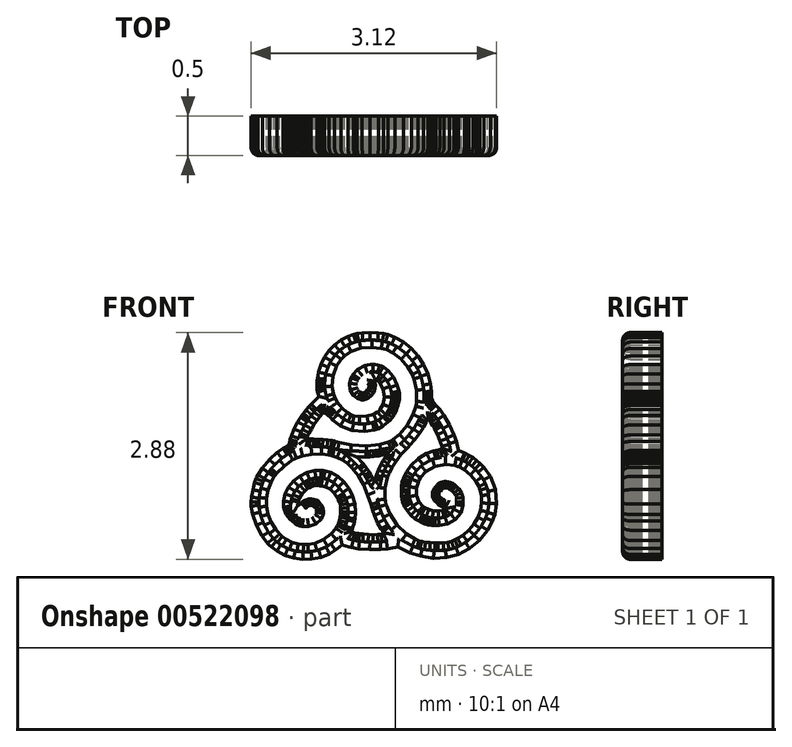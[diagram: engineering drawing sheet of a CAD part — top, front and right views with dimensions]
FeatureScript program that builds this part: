
annotation { "Feature Type Name" : "Feature", "Feature Type Description" : "" }
export const myFeature = defineFeature(function(context is Context, id is Id, definition is map)
    precondition{}
    {
        {
            var Q0;
            Q0=qCreatedBy(makeId("Front.planeOp"),FACE);
            var sketch = newSketch(context, id + "F0", { "sketchPlane" : qUnion([Q0])});
            skLineSegment(sketch, "E0", {"start": v(-0.23, 1.42) * mm, "end": v(-0.26, 1.42) * mm});
            skLineSegment(sketch, "E1", {"start": v(-0.26, 1.42) * mm, "end": v(-0.33, 1.4) * mm});
            skLineSegment(sketch, "E2", {"start": v(-0.33, 1.4) * mm, "end": v(-0.42, 1.34) * mm});
            skLineSegment(sketch, "E3", {"start": v(-0.42, 1.34) * mm, "end": v(-0.5, 1.28) * mm});
            skLineSegment(sketch, "E4", {"start": v(-0.5, 1.28) * mm, "end": v(-0.57, 1.21) * mm});
            skLineSegment(sketch, "E5", {"start": v(-0.57, 1.21) * mm, "end": v(-0.63, 1.13) * mm});
            skLineSegment(sketch, "E6", {"start": v(-0.63, 1.13) * mm, "end": v(-0.67, 1.04) * mm});
            skLineSegment(sketch, "E7", {"start": v(-0.67, 1.04) * mm, "end": v(-0.7, 0.94) * mm});
            skLineSegment(sketch, "E8", {"start": v(-0.7, 0.94) * mm, "end": v(-0.72, 0.86) * mm});
            skLineSegment(sketch, "E9", {"start": v(-0.72, 0.86) * mm, "end": v(-0.72, 0.83) * mm});
            skLineSegment(sketch, "E10", {"start": v(-0.72, 0.83) * mm, "end": v(-0.72, 0.82) * mm});
            skLineSegment(sketch, "E11", {"start": v(-0.72, 0.82) * mm, "end": v(-0.72, 0.8) * mm});
            skLineSegment(sketch, "E12", {"start": v(-0.72, 0.8) * mm, "end": v(-0.72, 0.75) * mm});
            skLineSegment(sketch, "E13", {"start": v(-0.72, 0.75) * mm, "end": v(-0.72, 0.71) * mm});
            skLineSegment(sketch, "E14", {"start": v(-0.72, 0.71) * mm, "end": v(-0.72, 0.7) * mm});
            skLineSegment(sketch, "E15", {"start": v(-0.72, 0.7) * mm, "end": v(-0.71, 0.69) * mm});
            skLineSegment(sketch, "E16", {"start": v(-0.71, 0.69) * mm, "end": v(-0.7, 0.63) * mm});
            skLineSegment(sketch, "E17", {"start": v(-0.7, 0.63) * mm, "end": v(-0.79, 0.54) * mm});
            skLineSegment(sketch, "E18", {"start": v(-0.79, 0.54) * mm, "end": v(-0.8, 0.53) * mm});
            skLineSegment(sketch, "E19", {"start": v(-0.8, 0.53) * mm, "end": v(-0.83, 0.5) * mm});
            skLineSegment(sketch, "E20", {"start": v(-0.83, 0.5) * mm, "end": v(-0.86, 0.46) * mm});
            skLineSegment(sketch, "E21", {"start": v(-0.86, 0.46) * mm, "end": v(-0.9, 0.42) * mm});
            skLineSegment(sketch, "E22", {"start": v(-0.9, 0.42) * mm, "end": v(-0.91, 0.4) * mm});
            skLineSegment(sketch, "E23", {"start": v(-0.91, 0.4) * mm, "end": v(-0.92, 0.38) * mm});
            skLineSegment(sketch, "E24", {"start": v(-0.92, 0.38) * mm, "end": v(-0.93, 0.36) * mm});
            skLineSegment(sketch, "E25", {"start": v(-0.93, 0.36) * mm, "end": v(-0.97, 0.3) * mm});
            skLineSegment(sketch, "E26", {"start": v(-0.97, 0.3) * mm, "end": v(-1.01, 0.22) * mm});
            skLineSegment(sketch, "E27", {"start": v(-1.01, 0.22) * mm, "end": v(-1.05, 0.13) * mm});
            skLineSegment(sketch, "E28", {"start": v(-1.05, 0.13) * mm, "end": v(-1.06, 0.08) * mm});
            skLineSegment(sketch, "E29", {"start": v(-1.06, 0.08) * mm, "end": v(-1.07, 0.06) * mm});
            skLineSegment(sketch, "E30", {"start": v(-1.07, 0.06) * mm, "end": v(-1.07, 0.06) * mm});
            skLineSegment(sketch, "E31", {"start": v(-1.07, 0.06) * mm, "end": v(-1.07, 0.04) * mm});
            skLineSegment(sketch, "E32", {"start": v(-1.07, 0.04) * mm, "end": v(-1.09, 0.02) * mm});
            skLineSegment(sketch, "E33", {"start": v(-1.09, 0.02) * mm, "end": v(-1.1, 0) * mm});
            skLineSegment(sketch, "E34", {"start": v(-1.1, 0) * mm, "end": v(-1.12, -0.01) * mm});
            skLineSegment(sketch, "E35", {"start": v(-1.12, -0.01) * mm, "end": v(-1.13, -0.02) * mm});
            skLineSegment(sketch, "E36", {"start": v(-1.13, -0.02) * mm, "end": v(-1.15, -0.03) * mm});
            skLineSegment(sketch, "E37", {"start": v(-1.15, -0.03) * mm, "end": v(-1.23, -0.08) * mm});
            skLineSegment(sketch, "E38", {"start": v(-1.23, -0.08) * mm, "end": v(-1.33, -0.17) * mm});
            skLineSegment(sketch, "E39", {"start": v(-1.33, -0.17) * mm, "end": v(-1.42, -0.28) * mm});
            skLineSegment(sketch, "E40", {"start": v(-1.42, -0.28) * mm, "end": v(-1.47, -0.37) * mm});
            skLineSegment(sketch, "E41", {"start": v(-1.47, -0.37) * mm, "end": v(-1.49, -0.4) * mm});
            skLineSegment(sketch, "E42", {"start": v(-1.49, -0.4) * mm, "end": v(-1.5, -0.41) * mm});
            skLineSegment(sketch, "E43", {"start": v(-1.5, -0.41) * mm, "end": v(-1.51, -0.47) * mm});
            skLineSegment(sketch, "E44", {"start": v(-1.51, -0.47) * mm, "end": v(-1.54, -0.56) * mm});
            skLineSegment(sketch, "E45", {"start": v(-1.54, -0.56) * mm, "end": v(-1.55, -0.65) * mm});
            skLineSegment(sketch, "E46", {"start": v(-1.55, -0.65) * mm, "end": v(-1.56, -0.7) * mm});
            skLineSegment(sketch, "E47", {"start": v(-1.56, -0.7) * mm, "end": v(-1.56, -0.73) * mm});
            skLineSegment(sketch, "E48", {"start": v(-1.56, -0.73) * mm, "end": v(-1.56, -0.76) * mm});
            skLineSegment(sketch, "E49", {"start": v(-1.56, -0.76) * mm, "end": v(-1.54, -0.86) * mm});
            skLineSegment(sketch, "E50", {"start": v(-1.54, -0.86) * mm, "end": v(-1.5, -1) * mm});
            skLineSegment(sketch, "E51", {"start": v(-1.5, -1) * mm, "end": v(-1.42, -1.14) * mm});
            skLineSegment(sketch, "E52", {"start": v(-1.42, -1.14) * mm, "end": v(-1.35, -1.24) * mm});
            skLineSegment(sketch, "E53", {"start": v(-1.35, -1.24) * mm, "end": v(-1.32, -1.26) * mm});
            skLineSegment(sketch, "E54", {"start": v(-1.32, -1.26) * mm, "end": v(-1.3, -1.28) * mm});
            skLineSegment(sketch, "E55", {"start": v(-1.3, -1.28) * mm, "end": v(-1.23, -1.34) * mm});
            skLineSegment(sketch, "E56", {"start": v(-1.23, -1.34) * mm, "end": v(-1.13, -1.39) * mm});
            skLineSegment(sketch, "E57", {"start": v(-1.13, -1.39) * mm, "end": v(-1.02, -1.43) * mm});
            skLineSegment(sketch, "E58", {"start": v(-1.02, -1.43) * mm, "end": v(-0.9, -1.44) * mm});
            skLineSegment(sketch, "E59", {"start": v(-0.9, -1.44) * mm, "end": v(-0.79, -1.44) * mm});
            skLineSegment(sketch, "E60", {"start": v(-0.79, -1.44) * mm, "end": v(-0.67, -1.41) * mm});
            skLineSegment(sketch, "E61", {"start": v(-0.67, -1.41) * mm, "end": v(-0.56, -1.37) * mm});
            skLineSegment(sketch, "E62", {"start": v(-0.56, -1.37) * mm, "end": v(-0.49, -1.32) * mm});
            skLineSegment(sketch, "E63", {"start": v(-0.49, -1.32) * mm, "end": v(-0.47, -1.3) * mm});
            skLineSegment(sketch, "E64", {"start": v(-0.47, -1.3) * mm, "end": v(-0.4, -1.26) * mm});
            skLineSegment(sketch, "E65", {"start": v(-0.4, -1.26) * mm, "end": v(-0.31, -1.28) * mm});
            skLineSegment(sketch, "E66", {"start": v(-0.31, -1.28) * mm, "end": v(-0.28, -1.3) * mm});
            skLineSegment(sketch, "E67", {"start": v(-0.28, -1.3) * mm, "end": v(-0.2, -1.3) * mm});
            skLineSegment(sketch, "E68", {"start": v(-0.2, -1.3) * mm, "end": v(-0.05, -1.32) * mm});
            skLineSegment(sketch, "E69", {"start": v(-0.05, -1.32) * mm, "end": v(0.09, -1.32) * mm});
            skLineSegment(sketch, "E70", {"start": v(0.09, -1.32) * mm, "end": v(0.17, -1.3) * mm});
            skLineSegment(sketch, "E71", {"start": v(0.17, -1.3) * mm, "end": v(0.2, -1.3) * mm});
            skLineSegment(sketch, "E72", {"start": v(0.2, -1.3) * mm, "end": v(0.3, -1.28) * mm});
            skLineSegment(sketch, "E73", {"start": v(0.3, -1.28) * mm, "end": v(0.42, -1.34) * mm});
            skLineSegment(sketch, "E74", {"start": v(0.42, -1.34) * mm, "end": v(0.46, -1.36) * mm});
            skLineSegment(sketch, "E75", {"start": v(0.46, -1.36) * mm, "end": v(0.6, -1.4) * mm});
            skLineSegment(sketch, "E76", {"start": v(0.6, -1.4) * mm, "end": v(0.76, -1.43) * mm});
            skLineSegment(sketch, "E77", {"start": v(0.76, -1.43) * mm, "end": v(0.92, -1.42) * mm});
            skLineSegment(sketch, "E78", {"start": v(0.92, -1.42) * mm, "end": v(1.08, -1.38) * mm});
            skLineSegment(sketch, "E79", {"start": v(1.08, -1.38) * mm, "end": v(1.22, -1.3) * mm});
            skLineSegment(sketch, "E80", {"start": v(1.22, -1.3) * mm, "end": v(1.34, -1.2) * mm});
            skLineSegment(sketch, "E81", {"start": v(1.34, -1.2) * mm, "end": v(1.44, -1.07) * mm});
            skLineSegment(sketch, "E82", {"start": v(1.44, -1.07) * mm, "end": v(1.5, -0.95) * mm});
            skLineSegment(sketch, "E83", {"start": v(1.5, -0.95) * mm, "end": v(1.52, -0.91) * mm});
            skLineSegment(sketch, "E84", {"start": v(1.52, -0.91) * mm, "end": v(1.54, -0.87) * mm});
            skLineSegment(sketch, "E85", {"start": v(1.54, -0.87) * mm, "end": v(1.56, -0.73) * mm});
            skLineSegment(sketch, "E86", {"start": v(1.56, -0.73) * mm, "end": v(1.54, -0.55) * mm});
            skLineSegment(sketch, "E87", {"start": v(1.54, -0.55) * mm, "end": v(1.48, -0.39) * mm});
            skLineSegment(sketch, "E88", {"start": v(1.48, -0.39) * mm, "end": v(1.4, -0.27) * mm});
            skLineSegment(sketch, "E89", {"start": v(1.4, -0.27) * mm, "end": v(1.37, -0.24) * mm});
            skLineSegment(sketch, "E90", {"start": v(1.37, -0.24) * mm, "end": v(1.35, -0.22) * mm});
            skLineSegment(sketch, "E91", {"start": v(1.35, -0.22) * mm, "end": v(1.3, -0.18) * mm});
            skLineSegment(sketch, "E92", {"start": v(1.3, -0.18) * mm, "end": v(1.26, -0.15) * mm});
            skLineSegment(sketch, "E93", {"start": v(1.26, -0.15) * mm, "end": v(1.21, -0.12) * mm});
            skLineSegment(sketch, "E94", {"start": v(1.21, -0.12) * mm, "end": v(1.17, -0.1) * mm});
            skLineSegment(sketch, "E95", {"start": v(1.17, -0.1) * mm, "end": v(1.15, -0.1) * mm});
            skLineSegment(sketch, "E96", {"start": v(1.15, -0.1) * mm, "end": v(1.07, -0.06) * mm});
            skLineSegment(sketch, "E97", {"start": v(1.07, -0.06) * mm, "end": v(1.06, 0.03) * mm});
            skLineSegment(sketch, "E98", {"start": v(1.06, 0.03) * mm, "end": v(1.05, 0.06) * mm});
            skLineSegment(sketch, "E99", {"start": v(1.05, 0.06) * mm, "end": v(1.02, 0.14) * mm});
            skLineSegment(sketch, "E100", {"start": v(1.02, 0.14) * mm, "end": v(0.96, 0.27) * mm});
            skLineSegment(sketch, "E101", {"start": v(0.96, 0.27) * mm, "end": v(0.9, 0.39) * mm});
            skLineSegment(sketch, "E102", {"start": v(0.9, 0.39) * mm, "end": v(0.84, 0.46) * mm});
            skLineSegment(sketch, "E103", {"start": v(0.84, 0.46) * mm, "end": v(0.82, 0.49) * mm});
            skLineSegment(sketch, "E104", {"start": v(0.82, 0.49) * mm, "end": v(0.8, 0.5) * mm});
            skLineSegment(sketch, "E105", {"start": v(0.8, 0.5) * mm, "end": v(0.79, 0.52) * mm});
            skLineSegment(sketch, "E106", {"start": v(0.79, 0.52) * mm, "end": v(0.77, 0.54) * mm});
            skLineSegment(sketch, "E107", {"start": v(0.77, 0.54) * mm, "end": v(0.75, 0.56) * mm});
            skLineSegment(sketch, "E108", {"start": v(0.75, 0.56) * mm, "end": v(0.74, 0.58) * mm});
            skLineSegment(sketch, "E109", {"start": v(0.74, 0.58) * mm, "end": v(0.74, 0.6) * mm});
            skLineSegment(sketch, "E110", {"start": v(0.74, 0.6) * mm, "end": v(0.73, 0.61) * mm});
            skLineSegment(sketch, "E111", {"start": v(0.73, 0.61) * mm, "end": v(0.73, 0.63) * mm});
            skLineSegment(sketch, "E112", {"start": v(0.73, 0.63) * mm, "end": v(0.73, 0.65) * mm});
            skLineSegment(sketch, "E113", {"start": v(0.73, 0.65) * mm, "end": v(0.73, 0.66) * mm});
            skLineSegment(sketch, "E114", {"start": v(0.73, 0.66) * mm, "end": v(0.73, 0.7) * mm});
            skLineSegment(sketch, "E115", {"start": v(0.73, 0.7) * mm, "end": v(0.72, 0.8) * mm});
            skLineSegment(sketch, "E116", {"start": v(0.72, 0.8) * mm, "end": v(0.69, 0.92) * mm});
            skLineSegment(sketch, "E117", {"start": v(0.69, 0.92) * mm, "end": v(0.63, 1.03) * mm});
            skLineSegment(sketch, "E118", {"start": v(0.63, 1.03) * mm, "end": v(0.56, 1.14) * mm});
            skLineSegment(sketch, "E119", {"start": v(0.56, 1.14) * mm, "end": v(0.48, 1.24) * mm});
            skLineSegment(sketch, "E120", {"start": v(0.48, 1.24) * mm, "end": v(0.38, 1.32) * mm});
            skLineSegment(sketch, "E121", {"start": v(0.38, 1.32) * mm, "end": v(0.27, 1.38) * mm});
            skLineSegment(sketch, "E122", {"start": v(0.27, 1.38) * mm, "end": v(0.18, 1.41) * mm});
            skLineSegment(sketch, "E123", {"start": v(0.18, 1.41) * mm, "end": v(0.15, 1.42) * mm});
            skLineSegment(sketch, "E124", {"start": v(0.15, 1.42) * mm, "end": v(0.13, 1.43) * mm});
            skLineSegment(sketch, "E125", {"start": v(0.13, 1.43) * mm, "end": v(0.06, 1.44) * mm});
            skLineSegment(sketch, "E126", {"start": v(0.06, 1.44) * mm, "end": v(-0.05, 1.44) * mm});
            skLineSegment(sketch, "E127", {"start": v(-0.05, 1.44) * mm, "end": v(-0.15, 1.44) * mm});
            skLineSegment(sketch, "E128", {"start": v(-0.15, 1.44) * mm, "end": v(-0.21, 1.43) * mm});
            skLineSegment(sketch, "E129", {"start": v(-0.21, 1.43) * mm, "end": v(-0.23, 1.42) * mm});
            skLineSegment(sketch, "E130", {"start": v(0.13, 1.23) * mm, "end": v(0.16, 1.22) * mm});
            skLineSegment(sketch, "E131", {"start": v(0.16, 1.22) * mm, "end": v(0.24, 1.18) * mm});
            skLineSegment(sketch, "E132", {"start": v(0.24, 1.18) * mm, "end": v(0.35, 1.1) * mm});
            skLineSegment(sketch, "E133", {"start": v(0.35, 1.1) * mm, "end": v(0.44, 1) * mm});
            skLineSegment(sketch, "E134", {"start": v(0.44, 1) * mm, "end": v(0.49, 0.9) * mm});
            skLineSegment(sketch, "E135", {"start": v(0.49, 0.9) * mm, "end": v(0.5, 0.88) * mm});
            skLineSegment(sketch, "E136", {"start": v(0.5, 0.88) * mm, "end": v(0.5, 0.85) * mm});
            skLineSegment(sketch, "E137", {"start": v(0.5, 0.85) * mm, "end": v(0.54, 0.7) * mm});
            skLineSegment(sketch, "E138", {"start": v(0.54, 0.7) * mm, "end": v(0.54, 0.57) * mm});
            skLineSegment(sketch, "E139", {"start": v(0.54, 0.57) * mm, "end": v(0.54, 0.54) * mm});
            skLineSegment(sketch, "E140", {"start": v(0.54, 0.54) * mm, "end": v(0.53, 0.5) * mm});
            skLineSegment(sketch, "E141", {"start": v(0.53, 0.5) * mm, "end": v(0.5, 0.4) * mm});
            skLineSegment(sketch, "E142", {"start": v(0.5, 0.4) * mm, "end": v(0.42, 0.26) * mm});
            skLineSegment(sketch, "E143", {"start": v(0.42, 0.26) * mm, "end": v(0.32, 0.15) * mm});
            skLineSegment(sketch, "E144", {"start": v(0.32, 0.15) * mm, "end": v(0.25, 0.08) * mm});
            skLineSegment(sketch, "E145", {"start": v(0.25, 0.08) * mm, "end": v(0.22, 0.07) * mm});
            skLineSegment(sketch, "E146", {"start": v(0.22, 0.07) * mm, "end": v(0.18, 0.05) * mm});
            skLineSegment(sketch, "E147", {"start": v(0.18, 0.05) * mm, "end": v(0.08, 0.02) * mm});
            skLineSegment(sketch, "E148", {"start": v(0.08, 0.02) * mm, "end": v(-0.1, 0) * mm});
            skLineSegment(sketch, "E149", {"start": v(-0.1, 0) * mm, "end": v(-0.28, 0.02) * mm});
            skLineSegment(sketch, "E150", {"start": v(-0.28, 0.02) * mm, "end": v(-0.44, 0.05) * mm});
            skLineSegment(sketch, "E151", {"start": v(-0.44, 0.05) * mm, "end": v(-0.5, 0.06) * mm});
            skLineSegment(sketch, "E152", {"start": v(-0.5, 0.06) * mm, "end": v(-0.5, 0.06) * mm});
            skLineSegment(sketch, "E153", {"start": v(-0.5, 0.06) * mm, "end": v(-0.53, 0.07) * mm});
            skLineSegment(sketch, "E154", {"start": v(-0.53, 0.07) * mm, "end": v(-0.59, 0.08) * mm});
            skLineSegment(sketch, "E155", {"start": v(-0.59, 0.08) * mm, "end": v(-0.65, 0.08) * mm});
            skLineSegment(sketch, "E156", {"start": v(-0.65, 0.08) * mm, "end": v(-0.7, 0.09) * mm});
            skLineSegment(sketch, "E157", {"start": v(-0.7, 0.09) * mm, "end": v(-0.7, 0.09) * mm});
            skLineSegment(sketch, "E158", {"start": v(-0.7, 0.09) * mm, "end": v(-0.72, 0.09) * mm});
            skLineSegment(sketch, "E159", {"start": v(-0.72, 0.09) * mm, "end": v(-0.76, 0.09) * mm});
            skLineSegment(sketch, "E160", {"start": v(-0.76, 0.09) * mm, "end": v(-0.8, 0.1) * mm});
            skLineSegment(sketch, "E161", {"start": v(-0.8, 0.1) * mm, "end": v(-0.84, 0.1) * mm});
            skLineSegment(sketch, "E162", {"start": v(-0.84, 0.1) * mm, "end": v(-0.85, 0.1) * mm});
            skLineSegment(sketch, "E163", {"start": v(-0.85, 0.1) * mm, "end": v(-0.85, 0.1) * mm});
            skLineSegment(sketch, "E164", {"start": v(-0.85, 0.1) * mm, "end": v(-0.84, 0.12) * mm});
            skLineSegment(sketch, "E165", {"start": v(-0.84, 0.12) * mm, "end": v(-0.82, 0.17) * mm});
            skLineSegment(sketch, "E166", {"start": v(-0.82, 0.17) * mm, "end": v(-0.8, 0.22) * mm});
            skLineSegment(sketch, "E167", {"start": v(-0.8, 0.22) * mm, "end": v(-0.76, 0.27) * mm});
            skLineSegment(sketch, "E168", {"start": v(-0.76, 0.27) * mm, "end": v(-0.72, 0.33) * mm});
            skLineSegment(sketch, "E169", {"start": v(-0.72, 0.33) * mm, "end": v(-0.69, 0.37) * mm});
            skLineSegment(sketch, "E170", {"start": v(-0.69, 0.37) * mm, "end": v(-0.66, 0.4) * mm});
            skLineSegment(sketch, "E171", {"start": v(-0.66, 0.4) * mm, "end": v(-0.64, 0.42) * mm});
            skLineSegment(sketch, "E172", {"start": v(-0.64, 0.42) * mm, "end": v(-0.64, 0.42) * mm});
            skLineSegment(sketch, "E173", {"start": v(-0.64, 0.42) * mm, "end": v(-0.63, 0.43) * mm});
            skLineSegment(sketch, "E174", {"start": v(-0.63, 0.43) * mm, "end": v(-0.62, 0.42) * mm});
            skLineSegment(sketch, "E175", {"start": v(-0.62, 0.42) * mm, "end": v(-0.6, 0.4) * mm});
            skLineSegment(sketch, "E176", {"start": v(-0.6, 0.4) * mm, "end": v(-0.58, 0.39) * mm});
            skLineSegment(sketch, "E177", {"start": v(-0.58, 0.39) * mm, "end": v(-0.56, 0.37) * mm});
            skLineSegment(sketch, "E178", {"start": v(-0.56, 0.37) * mm, "end": v(-0.55, 0.36) * mm});
            skLineSegment(sketch, "E179", {"start": v(-0.55, 0.36) * mm, "end": v(-0.52, 0.33) * mm});
            skLineSegment(sketch, "E180", {"start": v(-0.52, 0.33) * mm, "end": v(-0.42, 0.26) * mm});
            skLineSegment(sketch, "E181", {"start": v(-0.42, 0.26) * mm, "end": v(-0.28, 0.2) * mm});
            skLineSegment(sketch, "E182", {"start": v(-0.28, 0.2) * mm, "end": v(-0.12, 0.18) * mm});
            skLineSegment(sketch, "E183", {"start": v(-0.12, 0.18) * mm, "end": v(0, 0.2) * mm});
            skLineSegment(sketch, "E184", {"start": v(0, 0.2) * mm, "end": v(0.04, 0.21) * mm});
            skLineSegment(sketch, "E185", {"start": v(0.04, 0.21) * mm, "end": v(0.06, 0.22) * mm});
            skLineSegment(sketch, "E186", {"start": v(0.06, 0.22) * mm, "end": v(0.12, 0.25) * mm});
            skLineSegment(sketch, "E187", {"start": v(0.12, 0.25) * mm, "end": v(0.18, 0.3) * mm});
            skLineSegment(sketch, "E188", {"start": v(0.18, 0.3) * mm, "end": v(0.2, 0.32) * mm});
            skLineSegment(sketch, "E189", {"start": v(0.2, 0.32) * mm, "end": v(0.2, 0.33) * mm});
            skLineSegment(sketch, "E190", {"start": v(0.2, 0.33) * mm, "end": v(0.23, 0.36) * mm});
            skLineSegment(sketch, "E191", {"start": v(0.23, 0.36) * mm, "end": v(0.26, 0.4) * mm});
            skLineSegment(sketch, "E192", {"start": v(0.26, 0.4) * mm, "end": v(0.28, 0.44) * mm});
            skLineSegment(sketch, "E193", {"start": v(0.28, 0.44) * mm, "end": v(0.3, 0.48) * mm});
            skLineSegment(sketch, "E194", {"start": v(0.3, 0.48) * mm, "end": v(0.3, 0.5) * mm});
            skLineSegment(sketch, "E195", {"start": v(0.3, 0.5) * mm, "end": v(0.3, 0.5) * mm});
            skLineSegment(sketch, "E196", {"start": v(0.3, 0.5) * mm, "end": v(0.32, 0.55) * mm});
            skLineSegment(sketch, "E197", {"start": v(0.32, 0.55) * mm, "end": v(0.32, 0.6) * mm});
            skLineSegment(sketch, "E198", {"start": v(0.32, 0.6) * mm, "end": v(0.33, 0.63) * mm});
            skLineSegment(sketch, "E199", {"start": v(0.33, 0.63) * mm, "end": v(0.32, 0.66) * mm});
            skLineSegment(sketch, "E200", {"start": v(0.32, 0.66) * mm, "end": v(0.32, 0.67) * mm});
            skLineSegment(sketch, "E201", {"start": v(0.32, 0.67) * mm, "end": v(0.32, 0.7) * mm});
            skLineSegment(sketch, "E202", {"start": v(0.32, 0.7) * mm, "end": v(0.3, 0.78) * mm});
            skLineSegment(sketch, "E203", {"start": v(0.3, 0.78) * mm, "end": v(0.25, 0.88) * mm});
            skLineSegment(sketch, "E204", {"start": v(0.25, 0.88) * mm, "end": v(0.18, 0.96) * mm});
            skLineSegment(sketch, "E205", {"start": v(0.18, 0.96) * mm, "end": v(0.12, 1) * mm});
            skLineSegment(sketch, "E206", {"start": v(0.12, 1) * mm, "end": v(0.1, 1.01) * mm});
            skLineSegment(sketch, "E207", {"start": v(0.1, 1.01) * mm, "end": v(0.07, 1.03) * mm});
            skLineSegment(sketch, "E208", {"start": v(0.07, 1.03) * mm, "end": v(0, 1.04) * mm});
            skLineSegment(sketch, "E209", {"start": v(0, 1.04) * mm, "end": v(-0.12, 1.02) * mm});
            skLineSegment(sketch, "E210", {"start": v(-0.12, 1.02) * mm, "end": v(-0.2, 0.97) * mm});
            skLineSegment(sketch, "E211", {"start": v(-0.2, 0.97) * mm, "end": v(-0.27, 0.91) * mm});
            skLineSegment(sketch, "E212", {"start": v(-0.27, 0.91) * mm, "end": v(-0.28, 0.89) * mm});
            skLineSegment(sketch, "E213", {"start": v(-0.28, 0.89) * mm, "end": v(-0.29, 0.87) * mm});
            skLineSegment(sketch, "E214", {"start": v(-0.29, 0.87) * mm, "end": v(-0.3, 0.8) * mm});
            skLineSegment(sketch, "E215", {"start": v(-0.3, 0.8) * mm, "end": v(-0.3, 0.71) * mm});
            skLineSegment(sketch, "E216", {"start": v(-0.3, 0.71) * mm, "end": v(-0.26, 0.64) * mm});
            skLineSegment(sketch, "E217", {"start": v(-0.26, 0.64) * mm, "end": v(-0.2, 0.6) * mm});
            skLineSegment(sketch, "E218", {"start": v(-0.2, 0.6) * mm, "end": v(-0.2, 0.6) * mm});
            skLineSegment(sketch, "E219", {"start": v(-0.2, 0.6) * mm, "end": v(-0.18, 0.6) * mm});
            skLineSegment(sketch, "E220", {"start": v(-0.18, 0.6) * mm, "end": v(-0.16, 0.59) * mm});
            skLineSegment(sketch, "E221", {"start": v(-0.16, 0.59) * mm, "end": v(-0.14, 0.59) * mm});
            skLineSegment(sketch, "E222", {"start": v(-0.14, 0.59) * mm, "end": v(-0.11, 0.59) * mm});
            skLineSegment(sketch, "E223", {"start": v(-0.11, 0.59) * mm, "end": v(-0.1, 0.6) * mm});
            skLineSegment(sketch, "E224", {"start": v(-0.1, 0.6) * mm, "end": v(-0.08, 0.6) * mm});
            skLineSegment(sketch, "E225", {"start": v(-0.08, 0.6) * mm, "end": v(-0.07, 0.6) * mm});
            skLineSegment(sketch, "E226", {"start": v(-0.07, 0.6) * mm, "end": v(-0.03, 0.63) * mm});
            skLineSegment(sketch, "E227", {"start": v(-0.03, 0.63) * mm, "end": v(0, 0.68) * mm});
            skLineSegment(sketch, "E228", {"start": v(0, 0.68) * mm, "end": v(0.02, 0.73) * mm});
            skLineSegment(sketch, "E229", {"start": v(0.02, 0.73) * mm, "end": v(0.02, 0.77) * mm});
            skLineSegment(sketch, "E230", {"start": v(0.02, 0.77) * mm, "end": v(0.02, 0.78) * mm});
            skLineSegment(sketch, "E231", {"start": v(0.02, 0.78) * mm, "end": v(0.02, 0.8) * mm});
            skLineSegment(sketch, "E232", {"start": v(0.02, 0.8) * mm, "end": v(0.02, 0.82) * mm});
            skLineSegment(sketch, "E233", {"start": v(0.02, 0.82) * mm, "end": v(0.02, 0.84) * mm});
            skLineSegment(sketch, "E234", {"start": v(0.02, 0.84) * mm, "end": v(0.04, 0.84) * mm});
            skLineSegment(sketch, "E235", {"start": v(0.04, 0.84) * mm, "end": v(0.06, 0.82) * mm});
            skLineSegment(sketch, "E236", {"start": v(0.06, 0.82) * mm, "end": v(0.06, 0.81) * mm});
            skLineSegment(sketch, "E237", {"start": v(0.06, 0.81) * mm, "end": v(0.08, 0.8) * mm});
            skLineSegment(sketch, "E238", {"start": v(0.08, 0.8) * mm, "end": v(0.12, 0.73) * mm});
            skLineSegment(sketch, "E239", {"start": v(0.12, 0.73) * mm, "end": v(0.13, 0.63) * mm});
            skLineSegment(sketch, "E240", {"start": v(0.13, 0.63) * mm, "end": v(0.12, 0.53) * mm});
            skLineSegment(sketch, "E241", {"start": v(0.12, 0.53) * mm, "end": v(0.08, 0.46) * mm});
            skLineSegment(sketch, "E242", {"start": v(0.08, 0.46) * mm, "end": v(0.06, 0.45) * mm});
            skLineSegment(sketch, "E243", {"start": v(0.06, 0.45) * mm, "end": v(0.05, 0.43) * mm});
            skLineSegment(sketch, "E244", {"start": v(0.05, 0.43) * mm, "end": v(0, 0.4) * mm});
            skLineSegment(sketch, "E245", {"start": v(0, 0.4) * mm, "end": v(-0.09, 0.38) * mm});
            skLineSegment(sketch, "E246", {"start": v(-0.09, 0.38) * mm, "end": v(-0.18, 0.37) * mm});
            skLineSegment(sketch, "E247", {"start": v(-0.18, 0.37) * mm, "end": v(-0.25, 0.38) * mm});
            skLineSegment(sketch, "E248", {"start": v(-0.25, 0.38) * mm, "end": v(-0.27, 0.39) * mm});
            skLineSegment(sketch, "E249", {"start": v(-0.27, 0.39) * mm, "end": v(-0.3, 0.4) * mm});
            skLineSegment(sketch, "E250", {"start": v(-0.3, 0.4) * mm, "end": v(-0.34, 0.42) * mm});
            skLineSegment(sketch, "E251", {"start": v(-0.34, 0.42) * mm, "end": v(-0.4, 0.48) * mm});
            skLineSegment(sketch, "E252", {"start": v(-0.4, 0.48) * mm, "end": v(-0.46, 0.55) * mm});
            skLineSegment(sketch, "E253", {"start": v(-0.46, 0.55) * mm, "end": v(-0.5, 0.6) * mm});
            skLineSegment(sketch, "E254", {"start": v(-0.5, 0.6) * mm, "end": v(-0.5, 0.63) * mm});
            skLineSegment(sketch, "E255", {"start": v(-0.5, 0.63) * mm, "end": v(-0.51, 0.66) * mm});
            skLineSegment(sketch, "E256", {"start": v(-0.51, 0.66) * mm, "end": v(-0.53, 0.76) * mm});
            skLineSegment(sketch, "E257", {"start": v(-0.53, 0.76) * mm, "end": v(-0.52, 0.9) * mm});
            skLineSegment(sketch, "E258", {"start": v(-0.52, 0.9) * mm, "end": v(-0.47, 1.02) * mm});
            skLineSegment(sketch, "E259", {"start": v(-0.47, 1.02) * mm, "end": v(-0.42, 1.1) * mm});
            skLineSegment(sketch, "E260", {"start": v(-0.42, 1.1) * mm, "end": v(-0.4, 1.12) * mm});
            skLineSegment(sketch, "E261", {"start": v(-0.4, 1.12) * mm, "end": v(-0.37, 1.15) * mm});
            skLineSegment(sketch, "E262", {"start": v(-0.37, 1.15) * mm, "end": v(-0.29, 1.2) * mm});
            skLineSegment(sketch, "E263", {"start": v(-0.29, 1.2) * mm, "end": v(-0.17, 1.24) * mm});
            skLineSegment(sketch, "E264", {"start": v(-0.17, 1.24) * mm, "end": v(-0.02, 1.25) * mm});
            skLineSegment(sketch, "E265", {"start": v(-0.02, 1.25) * mm, "end": v(0.1, 1.24) * mm});
            skLineSegment(sketch, "E266", {"start": v(0.1, 1.24) * mm, "end": v(0.13, 1.23) * mm});
            skLineSegment(sketch, "E267", {"start": v(0.77, 0.22) * mm, "end": v(0.78, 0.2) * mm});
            skLineSegment(sketch, "E268", {"start": v(0.78, 0.2) * mm, "end": v(0.8, 0.14) * mm});
            skLineSegment(sketch, "E269", {"start": v(0.8, 0.14) * mm, "end": v(0.84, 0.06) * mm});
            skLineSegment(sketch, "E270", {"start": v(0.84, 0.06) * mm, "end": v(0.87, 0) * mm});
            skLineSegment(sketch, "E271", {"start": v(0.87, 0) * mm, "end": v(0.87, -0.03) * mm});
            skLineSegment(sketch, "E272", {"start": v(0.87, -0.03) * mm, "end": v(0.87, -0.04) * mm});
            skLineSegment(sketch, "E273", {"start": v(0.87, -0.04) * mm, "end": v(0.87, -0.04) * mm});
            skLineSegment(sketch, "E274", {"start": v(0.87, -0.04) * mm, "end": v(0.84, -0.05) * mm});
            skLineSegment(sketch, "E275", {"start": v(0.84, -0.05) * mm, "end": v(0.8, -0.06) * mm});
            skLineSegment(sketch, "E276", {"start": v(0.8, -0.06) * mm, "end": v(0.8, -0.06) * mm});
            skLineSegment(sketch, "E277", {"start": v(0.8, -0.06) * mm, "end": v(0.76, -0.06) * mm});
            skLineSegment(sketch, "E278", {"start": v(0.76, -0.06) * mm, "end": v(0.67, -0.1) * mm});
            skLineSegment(sketch, "E279", {"start": v(0.67, -0.1) * mm, "end": v(0.56, -0.16) * mm});
            skLineSegment(sketch, "E280", {"start": v(0.56, -0.16) * mm, "end": v(0.47, -0.25) * mm});
            skLineSegment(sketch, "E281", {"start": v(0.47, -0.25) * mm, "end": v(0.42, -0.33) * mm});
            skLineSegment(sketch, "E282", {"start": v(0.42, -0.33) * mm, "end": v(0.4, -0.36) * mm});
            skLineSegment(sketch, "E283", {"start": v(0.4, -0.36) * mm, "end": v(0.4, -0.37) * mm});
            skLineSegment(sketch, "E284", {"start": v(0.4, -0.37) * mm, "end": v(0.37, -0.41) * mm});
            skLineSegment(sketch, "E285", {"start": v(0.37, -0.41) * mm, "end": v(0.36, -0.46) * mm});
            skLineSegment(sketch, "E286", {"start": v(0.36, -0.46) * mm, "end": v(0.35, -0.5) * mm});
            skLineSegment(sketch, "E287", {"start": v(0.35, -0.5) * mm, "end": v(0.35, -0.55) * mm});
            skLineSegment(sketch, "E288", {"start": v(0.35, -0.55) * mm, "end": v(0.35, -0.57) * mm});
            skLineSegment(sketch, "E289", {"start": v(0.35, -0.57) * mm, "end": v(0.35, -0.59) * mm});
            skLineSegment(sketch, "E290", {"start": v(0.35, -0.59) * mm, "end": v(0.35, -0.63) * mm});
            skLineSegment(sketch, "E291", {"start": v(0.35, -0.63) * mm, "end": v(0.36, -0.68) * mm});
            skLineSegment(sketch, "E292", {"start": v(0.36, -0.68) * mm, "end": v(0.37, -0.72) * mm});
            skLineSegment(sketch, "E293", {"start": v(0.37, -0.72) * mm, "end": v(0.38, -0.75) * mm});
            skLineSegment(sketch, "E294", {"start": v(0.38, -0.75) * mm, "end": v(0.38, -0.75) * mm});
            skLineSegment(sketch, "E295", {"start": v(0.38, -0.75) * mm, "end": v(0.4, -0.77) * mm});
            skLineSegment(sketch, "E296", {"start": v(0.4, -0.77) * mm, "end": v(0.42, -0.82) * mm});
            skLineSegment(sketch, "E297", {"start": v(0.42, -0.82) * mm, "end": v(0.47, -0.88) * mm});
            skLineSegment(sketch, "E298", {"start": v(0.47, -0.88) * mm, "end": v(0.52, -0.92) * mm});
            skLineSegment(sketch, "E299", {"start": v(0.52, -0.92) * mm, "end": v(0.57, -0.95) * mm});
            skLineSegment(sketch, "E300", {"start": v(0.57, -0.95) * mm, "end": v(0.6, -0.96) * mm});
            skLineSegment(sketch, "E301", {"start": v(0.6, -0.96) * mm, "end": v(0.6, -0.97) * mm});
            skLineSegment(sketch, "E302", {"start": v(0.6, -0.97) * mm, "end": v(0.64, -0.99) * mm});
            skLineSegment(sketch, "E303", {"start": v(0.64, -0.99) * mm, "end": v(0.69, -1) * mm});
            skLineSegment(sketch, "E304", {"start": v(0.69, -1) * mm, "end": v(0.73, -1) * mm});
            skLineSegment(sketch, "E305", {"start": v(0.73, -1) * mm, "end": v(0.78, -1) * mm});
            skLineSegment(sketch, "E306", {"start": v(0.78, -1) * mm, "end": v(0.8, -1) * mm});
            skLineSegment(sketch, "E307", {"start": v(0.8, -1) * mm, "end": v(0.83, -1) * mm});
            skLineSegment(sketch, "E308", {"start": v(0.83, -1) * mm, "end": v(0.93, -1) * mm});
            skLineSegment(sketch, "E309", {"start": v(0.93, -1) * mm, "end": v(1.04, -0.94) * mm});
            skLineSegment(sketch, "E310", {"start": v(1.04, -0.94) * mm, "end": v(1.1, -0.85) * mm});
            skLineSegment(sketch, "E311", {"start": v(1.1, -0.85) * mm, "end": v(1.13, -0.76) * mm});
            skLineSegment(sketch, "E312", {"start": v(1.13, -0.76) * mm, "end": v(1.13, -0.73) * mm});
            skLineSegment(sketch, "E313", {"start": v(1.13, -0.73) * mm, "end": v(1.13, -0.7) * mm});
            skLineSegment(sketch, "E314", {"start": v(1.13, -0.7) * mm, "end": v(1.13, -0.65) * mm});
            skLineSegment(sketch, "E315", {"start": v(1.13, -0.65) * mm, "end": v(1.11, -0.6) * mm});
            skLineSegment(sketch, "E316", {"start": v(1.11, -0.6) * mm, "end": v(1.08, -0.54) * mm});
            skLineSegment(sketch, "E317", {"start": v(1.08, -0.54) * mm, "end": v(1.05, -0.5) * mm});
            skLineSegment(sketch, "E318", {"start": v(1.05, -0.5) * mm, "end": v(1.03, -0.5) * mm});
            skLineSegment(sketch, "E319", {"start": v(1.03, -0.5) * mm, "end": v(1.03, -0.5) * mm});
            skLineSegment(sketch, "E320", {"start": v(1.03, -0.5) * mm, "end": v(1, -0.47) * mm});
            skLineSegment(sketch, "E321", {"start": v(1, -0.47) * mm, "end": v(0.98, -0.46) * mm});
            skLineSegment(sketch, "E322", {"start": v(0.98, -0.46) * mm, "end": v(0.95, -0.45) * mm});
            skLineSegment(sketch, "E323", {"start": v(0.95, -0.45) * mm, "end": v(0.92, -0.45) * mm});
            skLineSegment(sketch, "E324", {"start": v(0.92, -0.45) * mm, "end": v(0.9, -0.45) * mm});
            skLineSegment(sketch, "E325", {"start": v(0.9, -0.45) * mm, "end": v(0.9, -0.45) * mm});
            skLineSegment(sketch, "E326", {"start": v(0.9, -0.45) * mm, "end": v(0.87, -0.45) * mm});
            skLineSegment(sketch, "E327", {"start": v(0.87, -0.45) * mm, "end": v(0.84, -0.46) * mm});
            skLineSegment(sketch, "E328", {"start": v(0.84, -0.46) * mm, "end": v(0.82, -0.48) * mm});
            skLineSegment(sketch, "E329", {"start": v(0.82, -0.48) * mm, "end": v(0.8, -0.5) * mm});
            skLineSegment(sketch, "E330", {"start": v(0.8, -0.5) * mm, "end": v(0.8, -0.5) * mm});
            skLineSegment(sketch, "E331", {"start": v(0.8, -0.5) * mm, "end": v(0.79, -0.51) * mm});
            skLineSegment(sketch, "E332", {"start": v(0.79, -0.51) * mm, "end": v(0.77, -0.53) * mm});
            skLineSegment(sketch, "E333", {"start": v(0.77, -0.53) * mm, "end": v(0.76, -0.56) * mm});
            skLineSegment(sketch, "E334", {"start": v(0.76, -0.56) * mm, "end": v(0.75, -0.58) * mm});
            skLineSegment(sketch, "E335", {"start": v(0.75, -0.58) * mm, "end": v(0.75, -0.6) * mm});
            skLineSegment(sketch, "E336", {"start": v(0.75, -0.6) * mm, "end": v(0.75, -0.61) * mm});
            skLineSegment(sketch, "E337", {"start": v(0.75, -0.61) * mm, "end": v(0.75, -0.62) * mm});
            skLineSegment(sketch, "E338", {"start": v(0.75, -0.62) * mm, "end": v(0.75, -0.65) * mm});
            skLineSegment(sketch, "E339", {"start": v(0.75, -0.65) * mm, "end": v(0.76, -0.67) * mm});
            skLineSegment(sketch, "E340", {"start": v(0.76, -0.67) * mm, "end": v(0.77, -0.7) * mm});
            skLineSegment(sketch, "E341", {"start": v(0.77, -0.7) * mm, "end": v(0.8, -0.72) * mm});
            skLineSegment(sketch, "E342", {"start": v(0.8, -0.72) * mm, "end": v(0.8, -0.73) * mm});
            skLineSegment(sketch, "E343", {"start": v(0.8, -0.73) * mm, "end": v(0.8, -0.73) * mm});
            skLineSegment(sketch, "E344", {"start": v(0.8, -0.73) * mm, "end": v(0.82, -0.75) * mm});
            skLineSegment(sketch, "E345", {"start": v(0.82, -0.75) * mm, "end": v(0.85, -0.76) * mm});
            skLineSegment(sketch, "E346", {"start": v(0.85, -0.76) * mm, "end": v(0.87, -0.78) * mm});
            skLineSegment(sketch, "E347", {"start": v(0.87, -0.78) * mm, "end": v(0.88, -0.78) * mm});
            skLineSegment(sketch, "E348", {"start": v(0.88, -0.78) * mm, "end": v(0.88, -0.78) * mm});
            skLineSegment(sketch, "E349", {"start": v(0.88, -0.78) * mm, "end": v(0.89, -0.78) * mm});
            skLineSegment(sketch, "E350", {"start": v(0.89, -0.78) * mm, "end": v(0.9, -0.78) * mm});
            skLineSegment(sketch, "E351", {"start": v(0.9, -0.78) * mm, "end": v(0.91, -0.8) * mm});
            skLineSegment(sketch, "E352", {"start": v(0.91, -0.8) * mm, "end": v(0.9, -0.8) * mm});
            skLineSegment(sketch, "E353", {"start": v(0.9, -0.8) * mm, "end": v(0.9, -0.81) * mm});
            skLineSegment(sketch, "E354", {"start": v(0.9, -0.81) * mm, "end": v(0.89, -0.81) * mm});
            skLineSegment(sketch, "E355", {"start": v(0.89, -0.81) * mm, "end": v(0.87, -0.82) * mm});
            skLineSegment(sketch, "E356", {"start": v(0.87, -0.82) * mm, "end": v(0.82, -0.83) * mm});
            skLineSegment(sketch, "E357", {"start": v(0.82, -0.83) * mm, "end": v(0.76, -0.82) * mm});
            skLineSegment(sketch, "E358", {"start": v(0.76, -0.82) * mm, "end": v(0.7, -0.8) * mm});
            skLineSegment(sketch, "E359", {"start": v(0.7, -0.8) * mm, "end": v(0.65, -0.79) * mm});
            skLineSegment(sketch, "E360", {"start": v(0.65, -0.79) * mm, "end": v(0.64, -0.78) * mm});
            skLineSegment(sketch, "E361", {"start": v(0.64, -0.78) * mm, "end": v(0.62, -0.76) * mm});
            skLineSegment(sketch, "E362", {"start": v(0.62, -0.76) * mm, "end": v(0.58, -0.71) * mm});
            skLineSegment(sketch, "E363", {"start": v(0.58, -0.71) * mm, "end": v(0.54, -0.63) * mm});
            skLineSegment(sketch, "E364", {"start": v(0.54, -0.63) * mm, "end": v(0.54, -0.53) * mm});
            skLineSegment(sketch, "E365", {"start": v(0.54, -0.53) * mm, "end": v(0.56, -0.45) * mm});
            skLineSegment(sketch, "E366", {"start": v(0.56, -0.45) * mm, "end": v(0.58, -0.43) * mm});
            skLineSegment(sketch, "E367", {"start": v(0.58, -0.43) * mm, "end": v(0.6, -0.4) * mm});
            skLineSegment(sketch, "E368", {"start": v(0.6, -0.4) * mm, "end": v(0.66, -0.32) * mm});
            skLineSegment(sketch, "E369", {"start": v(0.66, -0.32) * mm, "end": v(0.77, -0.26) * mm});
            skLineSegment(sketch, "E370", {"start": v(0.77, -0.26) * mm, "end": v(0.91, -0.24) * mm});
            skLineSegment(sketch, "E371", {"start": v(0.91, -0.24) * mm, "end": v(1.03, -0.25) * mm});
            skLineSegment(sketch, "E372", {"start": v(1.03, -0.25) * mm, "end": v(1.07, -0.26) * mm});
            skLineSegment(sketch, "E373", {"start": v(1.07, -0.26) * mm, "end": v(1.09, -0.27) * mm});
            skLineSegment(sketch, "E374", {"start": v(1.09, -0.27) * mm, "end": v(1.15, -0.3) * mm});
            skLineSegment(sketch, "E375", {"start": v(1.15, -0.3) * mm, "end": v(1.23, -0.37) * mm});
            skLineSegment(sketch, "E376", {"start": v(1.23, -0.37) * mm, "end": v(1.3, -0.45) * mm});
            skLineSegment(sketch, "E377", {"start": v(1.3, -0.45) * mm, "end": v(1.33, -0.52) * mm});
            skLineSegment(sketch, "E378", {"start": v(1.33, -0.52) * mm, "end": v(1.34, -0.54) * mm});
            skLineSegment(sketch, "E379", {"start": v(1.34, -0.54) * mm, "end": v(1.35, -0.56) * mm});
            skLineSegment(sketch, "E380", {"start": v(1.35, -0.56) * mm, "end": v(1.36, -0.63) * mm});
            skLineSegment(sketch, "E381", {"start": v(1.36, -0.63) * mm, "end": v(1.37, -0.72) * mm});
            skLineSegment(sketch, "E382", {"start": v(1.37, -0.72) * mm, "end": v(1.35, -0.82) * mm});
            skLineSegment(sketch, "E383", {"start": v(1.35, -0.82) * mm, "end": v(1.32, -0.9) * mm});
            skLineSegment(sketch, "E384", {"start": v(1.32, -0.9) * mm, "end": v(1.27, -1) * mm});
            skLineSegment(sketch, "E385", {"start": v(1.27, -1) * mm, "end": v(1.2, -1.07) * mm});
            skLineSegment(sketch, "E386", {"start": v(1.2, -1.07) * mm, "end": v(1.13, -1.13) * mm});
            skLineSegment(sketch, "E387", {"start": v(1.13, -1.13) * mm, "end": v(1.06, -1.18) * mm});
            skLineSegment(sketch, "E388", {"start": v(1.06, -1.18) * mm, "end": v(1.04, -1.19) * mm});
            skLineSegment(sketch, "E389", {"start": v(1.04, -1.19) * mm, "end": v(1.03, -1.2) * mm});
            skLineSegment(sketch, "E390", {"start": v(1.03, -1.2) * mm, "end": v(0.99, -1.21) * mm});
            skLineSegment(sketch, "E391", {"start": v(0.99, -1.21) * mm, "end": v(0.94, -1.22) * mm});
            skLineSegment(sketch, "E392", {"start": v(0.94, -1.22) * mm, "end": v(0.88, -1.23) * mm});
            skLineSegment(sketch, "E393", {"start": v(0.88, -1.23) * mm, "end": v(0.82, -1.23) * mm});
            skLineSegment(sketch, "E394", {"start": v(0.82, -1.23) * mm, "end": v(0.8, -1.23) * mm});
            skLineSegment(sketch, "E395", {"start": v(0.8, -1.23) * mm, "end": v(0.77, -1.23) * mm});
            skLineSegment(sketch, "E396", {"start": v(0.77, -1.23) * mm, "end": v(0.72, -1.23) * mm});
            skLineSegment(sketch, "E397", {"start": v(0.72, -1.23) * mm, "end": v(0.66, -1.22) * mm});
            skLineSegment(sketch, "E398", {"start": v(0.66, -1.22) * mm, "end": v(0.6, -1.21) * mm});
            skLineSegment(sketch, "E399", {"start": v(0.6, -1.21) * mm, "end": v(0.57, -1.2) * mm});
            skLineSegment(sketch, "E400", {"start": v(0.57, -1.2) * mm, "end": v(0.56, -1.2) * mm});
            skLineSegment(sketch, "E401", {"start": v(0.56, -1.2) * mm, "end": v(0.52, -1.18) * mm});
            skLineSegment(sketch, "E402", {"start": v(0.52, -1.18) * mm, "end": v(0.42, -1.12) * mm});
            skLineSegment(sketch, "E403", {"start": v(0.42, -1.12) * mm, "end": v(0.3, -1) * mm});
            skLineSegment(sketch, "E404", {"start": v(0.3, -1) * mm, "end": v(0.2, -0.86) * mm});
            skLineSegment(sketch, "E405", {"start": v(0.2, -0.86) * mm, "end": v(0.16, -0.74) * mm});
            skLineSegment(sketch, "E406", {"start": v(0.16, -0.74) * mm, "end": v(0.15, -0.7) * mm});
            skLineSegment(sketch, "E407", {"start": v(0.15, -0.7) * mm, "end": v(0.14, -0.68) * mm});
            skLineSegment(sketch, "E408", {"start": v(0.14, -0.68) * mm, "end": v(0.14, -0.54) * mm});
            skLineSegment(sketch, "E409", {"start": v(0.14, -0.54) * mm, "end": v(0.18, -0.4) * mm});
            skLineSegment(sketch, "E410", {"start": v(0.18, -0.4) * mm, "end": v(0.19, -0.36) * mm});
            skLineSegment(sketch, "E411", {"start": v(0.19, -0.36) * mm, "end": v(0.2, -0.34) * mm});
            skLineSegment(sketch, "E412", {"start": v(0.2, -0.34) * mm, "end": v(0.23, -0.27) * mm});
            skLineSegment(sketch, "E413", {"start": v(0.23, -0.27) * mm, "end": v(0.28, -0.2) * mm});
            skLineSegment(sketch, "E414", {"start": v(0.28, -0.2) * mm, "end": v(0.35, -0.11) * mm});
            skLineSegment(sketch, "E415", {"start": v(0.35, -0.11) * mm, "end": v(0.41, -0.04) * mm});
            skLineSegment(sketch, "E416", {"start": v(0.41, -0.04) * mm, "end": v(0.44, -0.01) * mm});
            skLineSegment(sketch, "E417", {"start": v(0.44, -0.01) * mm, "end": v(0.46, 0.01) * mm});
            skLineSegment(sketch, "E418", {"start": v(0.46, 0.01) * mm, "end": v(0.52, 0.08) * mm});
            skLineSegment(sketch, "E419", {"start": v(0.52, 0.08) * mm, "end": v(0.58, 0.16) * mm});
            skLineSegment(sketch, "E420", {"start": v(0.58, 0.16) * mm, "end": v(0.63, 0.24) * mm});
            skLineSegment(sketch, "E421", {"start": v(0.63, 0.24) * mm, "end": v(0.66, 0.28) * mm});
            skLineSegment(sketch, "E422", {"start": v(0.66, 0.28) * mm, "end": v(0.66, 0.3) * mm});
            skLineSegment(sketch, "E423", {"start": v(0.66, 0.3) * mm, "end": v(0.66, 0.3) * mm});
            skLineSegment(sketch, "E424", {"start": v(0.66, 0.3) * mm, "end": v(0.68, 0.32) * mm});
            skLineSegment(sketch, "E425", {"start": v(0.68, 0.32) * mm, "end": v(0.7, 0.33) * mm});
            skLineSegment(sketch, "E426", {"start": v(0.7, 0.33) * mm, "end": v(0.7, 0.33) * mm});
            skLineSegment(sketch, "E427", {"start": v(0.7, 0.33) * mm, "end": v(0.7, 0.32) * mm});
            skLineSegment(sketch, "E428", {"start": v(0.7, 0.32) * mm, "end": v(0.72, 0.3) * mm});
            skLineSegment(sketch, "E429", {"start": v(0.72, 0.3) * mm, "end": v(0.74, 0.26) * mm});
            skLineSegment(sketch, "E430", {"start": v(0.74, 0.26) * mm, "end": v(0.76, 0.23) * mm});
            skLineSegment(sketch, "E431", {"start": v(0.76, 0.23) * mm, "end": v(0.77, 0.22) * mm});
            skLineSegment(sketch, "E432", {"start": v(-0.55, -0.12) * mm, "end": v(-0.53, -0.13) * mm});
            skLineSegment(sketch, "E433", {"start": v(-0.53, -0.13) * mm, "end": v(-0.47, -0.14) * mm});
            skLineSegment(sketch, "E434", {"start": v(-0.47, -0.14) * mm, "end": v(-0.4, -0.18) * mm});
            skLineSegment(sketch, "E435", {"start": v(-0.4, -0.18) * mm, "end": v(-0.34, -0.22) * mm});
            skLineSegment(sketch, "E436", {"start": v(-0.34, -0.22) * mm, "end": v(-0.3, -0.27) * mm});
            skLineSegment(sketch, "E437", {"start": v(-0.3, -0.27) * mm, "end": v(-0.28, -0.28) * mm});
            skLineSegment(sketch, "E438", {"start": v(-0.28, -0.28) * mm, "end": v(-0.26, -0.3) * mm});
            skLineSegment(sketch, "E439", {"start": v(-0.26, -0.3) * mm, "end": v(-0.2, -0.38) * mm});
            skLineSegment(sketch, "E440", {"start": v(-0.2, -0.38) * mm, "end": v(-0.13, -0.49) * mm});
            skLineSegment(sketch, "E441", {"start": v(-0.13, -0.49) * mm, "end": v(-0.08, -0.62) * mm});
            skLineSegment(sketch, "E442", {"start": v(-0.08, -0.62) * mm, "end": v(-0.04, -0.74) * mm});
            skLineSegment(sketch, "E443", {"start": v(-0.04, -0.74) * mm, "end": v(-0.02, -0.79) * mm});
            skLineSegment(sketch, "E444", {"start": v(-0.02, -0.79) * mm, "end": v(-0.02, -0.81) * mm});
            skLineSegment(sketch, "E445", {"start": v(-0.02, -0.81) * mm, "end": v(0, -0.88) * mm});
            skLineSegment(sketch, "E446", {"start": v(0, -0.88) * mm, "end": v(0.05, -0.98) * mm});
            skLineSegment(sketch, "E447", {"start": v(0.05, -0.98) * mm, "end": v(0.1, -1.05) * mm});
            skLineSegment(sketch, "E448", {"start": v(0.1, -1.05) * mm, "end": v(0.11, -1.09) * mm});
            skLineSegment(sketch, "E449", {"start": v(0.11, -1.09) * mm, "end": v(0.12, -1.1) * mm});
            skLineSegment(sketch, "E450", {"start": v(0.12, -1.1) * mm, "end": v(0.12, -1.1) * mm});
            skLineSegment(sketch, "E451", {"start": v(0.12, -1.1) * mm, "end": v(0.13, -1.1) * mm});
            skLineSegment(sketch, "E452", {"start": v(0.13, -1.1) * mm, "end": v(0.12, -1.11) * mm});
            skLineSegment(sketch, "E453", {"start": v(0.12, -1.11) * mm, "end": v(0.09, -1.12) * mm});
            skLineSegment(sketch, "E454", {"start": v(0.09, -1.12) * mm, "end": v(0.05, -1.13) * mm});
            skLineSegment(sketch, "E455", {"start": v(0.05, -1.13) * mm, "end": v(0, -1.13) * mm});
            skLineSegment(sketch, "E456", {"start": v(0, -1.13) * mm, "end": v(-0.07, -1.13) * mm});
            skLineSegment(sketch, "E457", {"start": v(-0.07, -1.13) * mm, "end": v(-0.13, -1.12) * mm});
            skLineSegment(sketch, "E458", {"start": v(-0.13, -1.12) * mm, "end": v(-0.18, -1.11) * mm});
            skLineSegment(sketch, "E459", {"start": v(-0.18, -1.11) * mm, "end": v(-0.2, -1.11) * mm});
            skLineSegment(sketch, "E460", {"start": v(-0.2, -1.11) * mm, "end": v(-0.2, -1.1) * mm});
            skLineSegment(sketch, "E461", {"start": v(-0.2, -1.1) * mm, "end": v(-0.24, -1.1) * mm});
            skLineSegment(sketch, "E462", {"start": v(-0.24, -1.1) * mm, "end": v(-0.27, -1.1) * mm});
            skLineSegment(sketch, "E463", {"start": v(-0.27, -1.1) * mm, "end": v(-0.28, -1.08) * mm});
            skLineSegment(sketch, "E464", {"start": v(-0.28, -1.08) * mm, "end": v(-0.28, -1.07) * mm});
            skLineSegment(sketch, "E465", {"start": v(-0.28, -1.07) * mm, "end": v(-0.27, -1.07) * mm});
            skLineSegment(sketch, "E466", {"start": v(-0.27, -1.07) * mm, "end": v(-0.27, -1.06) * mm});
            skLineSegment(sketch, "E467", {"start": v(-0.27, -1.06) * mm, "end": v(-0.27, -1.05) * mm});
            skLineSegment(sketch, "E468", {"start": v(-0.27, -1.05) * mm, "end": v(-0.26, -1.02) * mm});
            skLineSegment(sketch, "E469", {"start": v(-0.26, -1.02) * mm, "end": v(-0.25, -0.99) * mm});
            skLineSegment(sketch, "E470", {"start": v(-0.25, -0.99) * mm, "end": v(-0.25, -0.96) * mm});
            skLineSegment(sketch, "E471", {"start": v(-0.25, -0.96) * mm, "end": v(-0.24, -0.95) * mm});
            skLineSegment(sketch, "E472", {"start": v(-0.24, -0.95) * mm, "end": v(-0.24, -0.93) * mm});
            skLineSegment(sketch, "E473", {"start": v(-0.24, -0.93) * mm, "end": v(-0.23, -0.85) * mm});
            skLineSegment(sketch, "E474", {"start": v(-0.23, -0.85) * mm, "end": v(-0.24, -0.74) * mm});
            skLineSegment(sketch, "E475", {"start": v(-0.24, -0.74) * mm, "end": v(-0.27, -0.63) * mm});
            skLineSegment(sketch, "E476", {"start": v(-0.27, -0.63) * mm, "end": v(-0.32, -0.54) * mm});
            skLineSegment(sketch, "E477", {"start": v(-0.32, -0.54) * mm, "end": v(-0.38, -0.45) * mm});
            skLineSegment(sketch, "E478", {"start": v(-0.38, -0.45) * mm, "end": v(-0.46, -0.39) * mm});
            skLineSegment(sketch, "E479", {"start": v(-0.46, -0.39) * mm, "end": v(-0.55, -0.34) * mm});
            skLineSegment(sketch, "E480", {"start": v(-0.55, -0.34) * mm, "end": v(-0.62, -0.32) * mm});
            skLineSegment(sketch, "E481", {"start": v(-0.62, -0.32) * mm, "end": v(-0.64, -0.31) * mm});
            skLineSegment(sketch, "E482", {"start": v(-0.64, -0.31) * mm, "end": v(-0.67, -0.3) * mm});
            skLineSegment(sketch, "E483", {"start": v(-0.67, -0.3) * mm, "end": v(-0.75, -0.31) * mm});
            skLineSegment(sketch, "E484", {"start": v(-0.75, -0.31) * mm, "end": v(-0.85, -0.34) * mm});
            skLineSegment(sketch, "E485", {"start": v(-0.85, -0.34) * mm, "end": v(-0.94, -0.38) * mm});
            skLineSegment(sketch, "E486", {"start": v(-0.94, -0.38) * mm, "end": v(-1.02, -0.45) * mm});
            skLineSegment(sketch, "E487", {"start": v(-1.02, -0.45) * mm, "end": v(-1.08, -0.52) * mm});
            skLineSegment(sketch, "E488", {"start": v(-1.08, -0.52) * mm, "end": v(-1.13, -0.6) * mm});
            skLineSegment(sketch, "E489", {"start": v(-1.13, -0.6) * mm, "end": v(-1.15, -0.7) * mm});
            skLineSegment(sketch, "E490", {"start": v(-1.15, -0.7) * mm, "end": v(-1.15, -0.78) * mm});
            skLineSegment(sketch, "E491", {"start": v(-1.15, -0.78) * mm, "end": v(-1.14, -0.8) * mm});
            skLineSegment(sketch, "E492", {"start": v(-1.14, -0.8) * mm, "end": v(-1.14, -0.8) * mm});
            skLineSegment(sketch, "E493", {"start": v(-1.14, -0.8) * mm, "end": v(-1.13, -0.83) * mm});
            skLineSegment(sketch, "E494", {"start": v(-1.13, -0.83) * mm, "end": v(-1.11, -0.87) * mm});
            skLineSegment(sketch, "E495", {"start": v(-1.11, -0.87) * mm, "end": v(-1.1, -0.9) * mm});
            skLineSegment(sketch, "E496", {"start": v(-1.1, -0.9) * mm, "end": v(-1.06, -0.93) * mm});
            skLineSegment(sketch, "E497", {"start": v(-1.06, -0.93) * mm, "end": v(-1.04, -0.96) * mm});
            skLineSegment(sketch, "E498", {"start": v(-1.04, -0.96) * mm, "end": v(-1, -0.98) * mm});
            skLineSegment(sketch, "E499", {"start": v(-1, -0.98) * mm, "end": v(-0.97, -1) * mm});
            skLineSegment(sketch, "E500", {"start": v(-0.97, -1) * mm, "end": v(-0.94, -1.01) * mm});
            skLineSegment(sketch, "E501", {"start": v(-0.94, -1.01) * mm, "end": v(-0.94, -1.02) * mm});
            skLineSegment(sketch, "E502", {"start": v(-0.94, -1.02) * mm, "end": v(-0.91, -1.02) * mm});
            skLineSegment(sketch, "E503", {"start": v(-0.91, -1.02) * mm, "end": v(-0.83, -1.02) * mm});
            skLineSegment(sketch, "E504", {"start": v(-0.83, -1.02) * mm, "end": v(-0.73, -1) * mm});
            skLineSegment(sketch, "E505", {"start": v(-0.73, -1) * mm, "end": v(-0.66, -0.93) * mm});
            skLineSegment(sketch, "E506", {"start": v(-0.66, -0.93) * mm, "end": v(-0.64, -0.86) * mm});
            skLineSegment(sketch, "E507", {"start": v(-0.64, -0.86) * mm, "end": v(-0.64, -0.84) * mm});
            skLineSegment(sketch, "E508", {"start": v(-0.64, -0.84) * mm, "end": v(-0.64, -0.82) * mm});
            skLineSegment(sketch, "E509", {"start": v(-0.64, -0.82) * mm, "end": v(-0.65, -0.79) * mm});
            skLineSegment(sketch, "E510", {"start": v(-0.65, -0.79) * mm, "end": v(-0.67, -0.74) * mm});
            skLineSegment(sketch, "E511", {"start": v(-0.67, -0.74) * mm, "end": v(-0.7, -0.7) * mm});
            skLineSegment(sketch, "E512", {"start": v(-0.7, -0.7) * mm, "end": v(-0.74, -0.69) * mm});
            skLineSegment(sketch, "E513", {"start": v(-0.74, -0.69) * mm, "end": v(-0.75, -0.68) * mm});
            skLineSegment(sketch, "E514", {"start": v(-0.75, -0.68) * mm, "end": v(-0.76, -0.68) * mm});
            skLineSegment(sketch, "E515", {"start": v(-0.76, -0.68) * mm, "end": v(-0.8, -0.67) * mm});
            skLineSegment(sketch, "E516", {"start": v(-0.8, -0.67) * mm, "end": v(-0.83, -0.68) * mm});
            skLineSegment(sketch, "E517", {"start": v(-0.83, -0.68) * mm, "end": v(-0.87, -0.7) * mm});
            skLineSegment(sketch, "E518", {"start": v(-0.87, -0.7) * mm, "end": v(-0.9, -0.71) * mm});
            skLineSegment(sketch, "E519", {"start": v(-0.9, -0.71) * mm, "end": v(-0.92, -0.72) * mm});
            skLineSegment(sketch, "E520", {"start": v(-0.92, -0.72) * mm, "end": v(-0.97, -0.76) * mm});
            skLineSegment(sketch, "E521", {"start": v(-0.97, -0.76) * mm, "end": v(-0.96, -0.71) * mm});
            skLineSegment(sketch, "E522", {"start": v(-0.96, -0.71) * mm, "end": v(-0.96, -0.7) * mm});
            skLineSegment(sketch, "E523", {"start": v(-0.96, -0.7) * mm, "end": v(-0.94, -0.66) * mm});
            skLineSegment(sketch, "E524", {"start": v(-0.94, -0.66) * mm, "end": v(-0.91, -0.61) * mm});
            skLineSegment(sketch, "E525", {"start": v(-0.91, -0.61) * mm, "end": v(-0.88, -0.57) * mm});
            skLineSegment(sketch, "E526", {"start": v(-0.88, -0.57) * mm, "end": v(-0.84, -0.54) * mm});
            skLineSegment(sketch, "E527", {"start": v(-0.84, -0.54) * mm, "end": v(-0.83, -0.54) * mm});
            skLineSegment(sketch, "E528", {"start": v(-0.83, -0.54) * mm, "end": v(-0.82, -0.53) * mm});
            skLineSegment(sketch, "E529", {"start": v(-0.82, -0.53) * mm, "end": v(-0.8, -0.52) * mm});
            skLineSegment(sketch, "E530", {"start": v(-0.8, -0.52) * mm, "end": v(-0.76, -0.5) * mm});
            skLineSegment(sketch, "E531", {"start": v(-0.76, -0.5) * mm, "end": v(-0.73, -0.5) * mm});
            skLineSegment(sketch, "E532", {"start": v(-0.73, -0.5) * mm, "end": v(-0.7, -0.5) * mm});
            skLineSegment(sketch, "E533", {"start": v(-0.7, -0.5) * mm, "end": v(-0.68, -0.5) * mm});
            skLineSegment(sketch, "E534", {"start": v(-0.68, -0.5) * mm, "end": v(-0.67, -0.5) * mm});
            skLineSegment(sketch, "E535", {"start": v(-0.67, -0.5) * mm, "end": v(-0.61, -0.52) * mm});
            skLineSegment(sketch, "E536", {"start": v(-0.61, -0.52) * mm, "end": v(-0.55, -0.55) * mm});
            skLineSegment(sketch, "E537", {"start": v(-0.55, -0.55) * mm, "end": v(-0.5, -0.6) * mm});
            skLineSegment(sketch, "E538", {"start": v(-0.5, -0.6) * mm, "end": v(-0.47, -0.65) * mm});
            skLineSegment(sketch, "E539", {"start": v(-0.47, -0.65) * mm, "end": v(-0.46, -0.67) * mm});
            skLineSegment(sketch, "E540", {"start": v(-0.46, -0.67) * mm, "end": v(-0.45, -0.68) * mm});
            skLineSegment(sketch, "E541", {"start": v(-0.45, -0.68) * mm, "end": v(-0.44, -0.71) * mm});
            skLineSegment(sketch, "E542", {"start": v(-0.44, -0.71) * mm, "end": v(-0.43, -0.75) * mm});
            skLineSegment(sketch, "E543", {"start": v(-0.43, -0.75) * mm, "end": v(-0.42, -0.8) * mm});
            skLineSegment(sketch, "E544", {"start": v(-0.42, -0.8) * mm, "end": v(-0.42, -0.84) * mm});
            skLineSegment(sketch, "E545", {"start": v(-0.42, -0.84) * mm, "end": v(-0.42, -0.85) * mm});
            skLineSegment(sketch, "E546", {"start": v(-0.42, -0.85) * mm, "end": v(-0.42, -0.86) * mm});
            skLineSegment(sketch, "E547", {"start": v(-0.42, -0.86) * mm, "end": v(-0.43, -0.9) * mm});
            skLineSegment(sketch, "E548", {"start": v(-0.43, -0.9) * mm, "end": v(-0.44, -0.95) * mm});
            skLineSegment(sketch, "E549", {"start": v(-0.44, -0.95) * mm, "end": v(-0.45, -0.98) * mm});
            skLineSegment(sketch, "E550", {"start": v(-0.45, -0.98) * mm, "end": v(-0.46, -1) * mm});
            skLineSegment(sketch, "E551", {"start": v(-0.46, -1) * mm, "end": v(-0.47, -1.02) * mm});
            skLineSegment(sketch, "E552", {"start": v(-0.47, -1.02) * mm, "end": v(-0.48, -1.04) * mm});
            skLineSegment(sketch, "E553", {"start": v(-0.48, -1.04) * mm, "end": v(-0.54, -1.12) * mm});
            skLineSegment(sketch, "E554", {"start": v(-0.54, -1.12) * mm, "end": v(-0.64, -1.19) * mm});
            skLineSegment(sketch, "E555", {"start": v(-0.64, -1.19) * mm, "end": v(-0.75, -1.24) * mm});
            skLineSegment(sketch, "E556", {"start": v(-0.75, -1.24) * mm, "end": v(-0.84, -1.25) * mm});
            skLineSegment(sketch, "E557", {"start": v(-0.84, -1.25) * mm, "end": v(-0.87, -1.25) * mm});
            skLineSegment(sketch, "E558", {"start": v(-0.87, -1.25) * mm, "end": v(-0.9, -1.25) * mm});
            skLineSegment(sketch, "E559", {"start": v(-0.9, -1.25) * mm, "end": v(-0.96, -1.25) * mm});
            skLineSegment(sketch, "E560", {"start": v(-0.96, -1.25) * mm, "end": v(-1.04, -1.22) * mm});
            skLineSegment(sketch, "E561", {"start": v(-1.04, -1.22) * mm, "end": v(-1.11, -1.19) * mm});
            skLineSegment(sketch, "E562", {"start": v(-1.11, -1.19) * mm, "end": v(-1.16, -1.15) * mm});
            skLineSegment(sketch, "E563", {"start": v(-1.16, -1.15) * mm, "end": v(-1.18, -1.14) * mm});
            skLineSegment(sketch, "E564", {"start": v(-1.18, -1.14) * mm, "end": v(-1.2, -1.12) * mm});
            skLineSegment(sketch, "E565", {"start": v(-1.2, -1.12) * mm, "end": v(-1.25, -1.06) * mm});
            skLineSegment(sketch, "E566", {"start": v(-1.25, -1.06) * mm, "end": v(-1.3, -0.97) * mm});
            skLineSegment(sketch, "E567", {"start": v(-1.3, -0.97) * mm, "end": v(-1.34, -0.87) * mm});
            skLineSegment(sketch, "E568", {"start": v(-1.34, -0.87) * mm, "end": v(-1.36, -0.77) * mm});
            skLineSegment(sketch, "E569", {"start": v(-1.36, -0.77) * mm, "end": v(-1.36, -0.66) * mm});
            skLineSegment(sketch, "E570", {"start": v(-1.36, -0.66) * mm, "end": v(-1.34, -0.56) * mm});
            skLineSegment(sketch, "E571", {"start": v(-1.34, -0.56) * mm, "end": v(-1.3, -0.46) * mm});
            skLineSegment(sketch, "E572", {"start": v(-1.3, -0.46) * mm, "end": v(-1.26, -0.39) * mm});
            skLineSegment(sketch, "E573", {"start": v(-1.26, -0.39) * mm, "end": v(-1.25, -0.37) * mm});
            skLineSegment(sketch, "E574", {"start": v(-1.25, -0.37) * mm, "end": v(-1.23, -0.35) * mm});
            skLineSegment(sketch, "E575", {"start": v(-1.23, -0.35) * mm, "end": v(-1.14, -0.25) * mm});
            skLineSegment(sketch, "E576", {"start": v(-1.14, -0.25) * mm, "end": v(-1.03, -0.17) * mm});
            skLineSegment(sketch, "E577", {"start": v(-1.03, -0.17) * mm, "end": v(-1, -0.16) * mm});
            skLineSegment(sketch, "E578", {"start": v(-1, -0.16) * mm, "end": v(-0.98, -0.15) * mm});
            skLineSegment(sketch, "E579", {"start": v(-0.98, -0.15) * mm, "end": v(-0.9, -0.12) * mm});
            skLineSegment(sketch, "E580", {"start": v(-0.9, -0.12) * mm, "end": v(-0.79, -0.1) * mm});
            skLineSegment(sketch, "E581", {"start": v(-0.79, -0.1) * mm, "end": v(-0.67, -0.1) * mm});
            skLineSegment(sketch, "E582", {"start": v(-0.67, -0.1) * mm, "end": v(-0.58, -0.11) * mm});
            skLineSegment(sketch, "E583", {"start": v(-0.58, -0.11) * mm, "end": v(-0.55, -0.12) * mm});
            skLineSegment(sketch, "E584", {"start": v(0.13, -0.17) * mm, "end": v(0.12, -0.18) * mm});
            skLineSegment(sketch, "E585", {"start": v(0.12, -0.18) * mm, "end": v(0.1, -0.23) * mm});
            skLineSegment(sketch, "E586", {"start": v(0.1, -0.23) * mm, "end": v(0.06, -0.3) * mm});
            skLineSegment(sketch, "E587", {"start": v(0.06, -0.3) * mm, "end": v(0.03, -0.37) * mm});
            skLineSegment(sketch, "E588", {"start": v(0.03, -0.37) * mm, "end": v(0.02, -0.4) * mm});
            skLineSegment(sketch, "E589", {"start": v(0.02, -0.4) * mm, "end": v(0.02, -0.42) * mm});
            skLineSegment(sketch, "E590", {"start": v(0.02, -0.42) * mm, "end": v(0.02, -0.42) * mm});
            skLineSegment(sketch, "E591", {"start": v(0.02, -0.42) * mm, "end": v(0.02, -0.44) * mm});
            skLineSegment(sketch, "E592", {"start": v(0.02, -0.44) * mm, "end": v(0, -0.44) * mm});
            skLineSegment(sketch, "E593", {"start": v(0, -0.44) * mm, "end": v(-0.01, -0.42) * mm});
            skLineSegment(sketch, "E594", {"start": v(-0.01, -0.42) * mm, "end": v(-0.03, -0.38) * mm});
            skLineSegment(sketch, "E595", {"start": v(-0.03, -0.38) * mm, "end": v(-0.04, -0.37) * mm});
            skLineSegment(sketch, "E596", {"start": v(-0.04, -0.37) * mm, "end": v(-0.04, -0.36) * mm});
            skLineSegment(sketch, "E597", {"start": v(-0.04, -0.36) * mm, "end": v(-0.06, -0.33) * mm});
            skLineSegment(sketch, "E598", {"start": v(-0.06, -0.33) * mm, "end": v(-0.08, -0.3) * mm});
            skLineSegment(sketch, "E599", {"start": v(-0.08, -0.3) * mm, "end": v(-0.12, -0.25) * mm});
            skLineSegment(sketch, "E600", {"start": v(-0.12, -0.25) * mm, "end": v(-0.14, -0.22) * mm});
            skLineSegment(sketch, "E601", {"start": v(-0.14, -0.22) * mm, "end": v(-0.15, -0.22) * mm});
            skLineSegment(sketch, "E602", {"start": v(-0.15, -0.22) * mm, "end": v(-0.22, -0.14) * mm});
            skLineSegment(sketch, "E603", {"start": v(-0.22, -0.14) * mm, "end": v(-0.1, -0.14) * mm});
            skLineSegment(sketch, "E604", {"start": v(-0.1, -0.14) * mm, "end": v(-0.09, -0.14) * mm});
            skLineSegment(sketch, "E605", {"start": v(-0.09, -0.14) * mm, "end": v(-0.05, -0.14) * mm});
            skLineSegment(sketch, "E606", {"start": v(-0.05, -0.14) * mm, "end": v(0, -0.13) * mm});
            skLineSegment(sketch, "E607", {"start": v(0, -0.13) * mm, "end": v(0.05, -0.13) * mm});
            skLineSegment(sketch, "E608", {"start": v(0.05, -0.13) * mm, "end": v(0.07, -0.12) * mm});
            skLineSegment(sketch, "E609", {"start": v(0.07, -0.12) * mm, "end": v(0.08, -0.12) * mm});
            skLineSegment(sketch, "E610", {"start": v(0.08, -0.12) * mm, "end": v(0.09, -0.12) * mm});
            skLineSegment(sketch, "E611", {"start": v(0.09, -0.12) * mm, "end": v(0.11, -0.11) * mm});
            skLineSegment(sketch, "E612", {"start": v(0.11, -0.11) * mm, "end": v(0.13, -0.1) * mm});
            skLineSegment(sketch, "E613", {"start": v(0.13, -0.1) * mm, "end": v(0.15, -0.1) * mm});
            skLineSegment(sketch, "E614", {"start": v(0.15, -0.1) * mm, "end": v(0.16, -0.1) * mm});
            skLineSegment(sketch, "E615", {"start": v(0.16, -0.1) * mm, "end": v(0.16, -0.11) * mm});
            skLineSegment(sketch, "E616", {"start": v(0.16, -0.11) * mm, "end": v(0.15, -0.13) * mm});
            skLineSegment(sketch, "E617", {"start": v(0.15, -0.13) * mm, "end": v(0.14, -0.14) * mm});
            skLineSegment(sketch, "E618", {"start": v(0.14, -0.14) * mm, "end": v(0.13, -0.16) * mm});
            skLineSegment(sketch, "E619", {"start": v(0.13, -0.16) * mm, "end": v(0.13, -0.17) * mm});
            skSolve(sketch);
        }
        {
            var Q0;
            Q0=makeQuery(id+"F0.imprint","IMPRINT",FACE,{"disambiguationData":[TD([[makeQuery(id+"F0.imprint","IMPRINT",EDGE,{"derivedFrom":sQuery(id+"F0.wireOp",EDGE,"E0")}),1.0]])]});
            extrude(context, id + "F1", {"entities" : qUnion([Q0]), "depth" : 0.5 * mm, "offsetDistance" : 25 * mm});
        }
        {
            var Q0;
            Q0=makeQuery(id+"F1.opExtrude","CAP_FACE",FACE,{"disambiguationData":[OSD([sQuery(id+"F0.wireOp",EDGE,"E0"),sQuery(id+"F0.wireOp",EDGE,"E1"),sQuery(id+"F0.wireOp",EDGE,"E2"),sQuery(id+"F0.wireOp",EDGE,"E3"),sQuery(id+"F0.wireOp",EDGE,"E4"),sQuery(id+"F0.wireOp",EDGE,"E5"),sQuery(id+"F0.wireOp",EDGE,"E6"),sQuery(id+"F0.wireOp",EDGE,"E7"),sQuery(id+"F0.wireOp",EDGE,"E8"),sQuery(id+"F0.wireOp",EDGE,"E9"),sQuery(id+"F0.wireOp",EDGE,"E10"),sQuery(id+"F0.wireOp",EDGE,"E11"),sQuery(id+"F0.wireOp",EDGE,"E12"),sQuery(id+"F0.wireOp",EDGE,"E13"),sQuery(id+"F0.wireOp",EDGE,"E14"),sQuery(id+"F0.wireOp",EDGE,"E15"),sQuery(id+"F0.wireOp",EDGE,"E16"),sQuery(id+"F0.wireOp",EDGE,"E17"),sQuery(id+"F0.wireOp",EDGE,"E18"),sQuery(id+"F0.wireOp",EDGE,"E19"),sQuery(id+"F0.wireOp",EDGE,"E20"),sQuery(id+"F0.wireOp",EDGE,"E21"),sQuery(id+"F0.wireOp",EDGE,"E22"),sQuery(id+"F0.wireOp",EDGE,"E23"),sQuery(id+"F0.wireOp",EDGE,"E24"),sQuery(id+"F0.wireOp",EDGE,"E25"),sQuery(id+"F0.wireOp",EDGE,"E26"),sQuery(id+"F0.wireOp",EDGE,"E27"),sQuery(id+"F0.wireOp",EDGE,"E28"),sQuery(id+"F0.wireOp",EDGE,"E29"),sQuery(id+"F0.wireOp",EDGE,"E30"),sQuery(id+"F0.wireOp",EDGE,"E31"),sQuery(id+"F0.wireOp",EDGE,"E32"),sQuery(id+"F0.wireOp",EDGE,"E33"),sQuery(id+"F0.wireOp",EDGE,"E34"),sQuery(id+"F0.wireOp",EDGE,"E35"),sQuery(id+"F0.wireOp",EDGE,"E36"),sQuery(id+"F0.wireOp",EDGE,"E37"),sQuery(id+"F0.wireOp",EDGE,"E38"),sQuery(id+"F0.wireOp",EDGE,"E39"),sQuery(id+"F0.wireOp",EDGE,"E40"),sQuery(id+"F0.wireOp",EDGE,"E41"),sQuery(id+"F0.wireOp",EDGE,"E42"),sQuery(id+"F0.wireOp",EDGE,"E43"),sQuery(id+"F0.wireOp",EDGE,"E44"),sQuery(id+"F0.wireOp",EDGE,"E45"),sQuery(id+"F0.wireOp",EDGE,"E46"),sQuery(id+"F0.wireOp",EDGE,"E47"),sQuery(id+"F0.wireOp",EDGE,"E48"),sQuery(id+"F0.wireOp",EDGE,"E49"),sQuery(id+"F0.wireOp",EDGE,"E50"),sQuery(id+"F0.wireOp",EDGE,"E51"),sQuery(id+"F0.wireOp",EDGE,"E52"),sQuery(id+"F0.wireOp",EDGE,"E53"),sQuery(id+"F0.wireOp",EDGE,"E54"),sQuery(id+"F0.wireOp",EDGE,"E55"),sQuery(id+"F0.wireOp",EDGE,"E56"),sQuery(id+"F0.wireOp",EDGE,"E57"),sQuery(id+"F0.wireOp",EDGE,"E58"),sQuery(id+"F0.wireOp",EDGE,"E59"),sQuery(id+"F0.wireOp",EDGE,"E60"),sQuery(id+"F0.wireOp",EDGE,"E61"),sQuery(id+"F0.wireOp",EDGE,"E62"),sQuery(id+"F0.wireOp",EDGE,"E63"),sQuery(id+"F0.wireOp",EDGE,"E64"),sQuery(id+"F0.wireOp",EDGE,"E65"),sQuery(id+"F0.wireOp",EDGE,"E66"),sQuery(id+"F0.wireOp",EDGE,"E67"),sQuery(id+"F0.wireOp",EDGE,"E68"),sQuery(id+"F0.wireOp",EDGE,"E69"),sQuery(id+"F0.wireOp",EDGE,"E70"),sQuery(id+"F0.wireOp",EDGE,"E71"),sQuery(id+"F0.wireOp",EDGE,"E72"),sQuery(id+"F0.wireOp",EDGE,"E73"),sQuery(id+"F0.wireOp",EDGE,"E74"),sQuery(id+"F0.wireOp",EDGE,"E75"),sQuery(id+"F0.wireOp",EDGE,"E76"),sQuery(id+"F0.wireOp",EDGE,"E77"),sQuery(id+"F0.wireOp",EDGE,"E78"),sQuery(id+"F0.wireOp",EDGE,"E79"),sQuery(id+"F0.wireOp",EDGE,"E80"),sQuery(id+"F0.wireOp",EDGE,"E81"),sQuery(id+"F0.wireOp",EDGE,"E82"),sQuery(id+"F0.wireOp",EDGE,"E83"),sQuery(id+"F0.wireOp",EDGE,"E84"),sQuery(id+"F0.wireOp",EDGE,"E85"),sQuery(id+"F0.wireOp",EDGE,"E86"),sQuery(id+"F0.wireOp",EDGE,"E87"),sQuery(id+"F0.wireOp",EDGE,"E88"),sQuery(id+"F0.wireOp",EDGE,"E89"),sQuery(id+"F0.wireOp",EDGE,"E90"),sQuery(id+"F0.wireOp",EDGE,"E91"),sQuery(id+"F0.wireOp",EDGE,"E92"),sQuery(id+"F0.wireOp",EDGE,"E93"),sQuery(id+"F0.wireOp",EDGE,"E94"),sQuery(id+"F0.wireOp",EDGE,"E95"),sQuery(id+"F0.wireOp",EDGE,"E96"),sQuery(id+"F0.wireOp",EDGE,"E97"),sQuery(id+"F0.wireOp",EDGE,"E98"),sQuery(id+"F0.wireOp",EDGE,"E99"),sQuery(id+"F0.wireOp",EDGE,"E100"),sQuery(id+"F0.wireOp",EDGE,"E101"),sQuery(id+"F0.wireOp",EDGE,"E102"),sQuery(id+"F0.wireOp",EDGE,"E103"),sQuery(id+"F0.wireOp",EDGE,"E104"),sQuery(id+"F0.wireOp",EDGE,"E105"),sQuery(id+"F0.wireOp",EDGE,"E106"),sQuery(id+"F0.wireOp",EDGE,"E107"),sQuery(id+"F0.wireOp",EDGE,"E108"),sQuery(id+"F0.wireOp",EDGE,"E109"),sQuery(id+"F0.wireOp",EDGE,"E110"),sQuery(id+"F0.wireOp",EDGE,"E111"),sQuery(id+"F0.wireOp",EDGE,"E112"),sQuery(id+"F0.wireOp",EDGE,"E113"),sQuery(id+"F0.wireOp",EDGE,"E114"),sQuery(id+"F0.wireOp",EDGE,"E115"),sQuery(id+"F0.wireOp",EDGE,"E116"),sQuery(id+"F0.wireOp",EDGE,"E117"),sQuery(id+"F0.wireOp",EDGE,"E118"),sQuery(id+"F0.wireOp",EDGE,"E119"),sQuery(id+"F0.wireOp",EDGE,"E120"),sQuery(id+"F0.wireOp",EDGE,"E121"),sQuery(id+"F0.wireOp",EDGE,"E122"),sQuery(id+"F0.wireOp",EDGE,"E123"),sQuery(id+"F0.wireOp",EDGE,"E124"),sQuery(id+"F0.wireOp",EDGE,"E125"),sQuery(id+"F0.wireOp",EDGE,"E126"),sQuery(id+"F0.wireOp",EDGE,"E127"),sQuery(id+"F0.wireOp",EDGE,"E128"),sQuery(id+"F0.wireOp",EDGE,"E129"),sQuery(id+"F0.wireOp",EDGE,"E130"),sQuery(id+"F0.wireOp",EDGE,"E131"),sQuery(id+"F0.wireOp",EDGE,"E132"),sQuery(id+"F0.wireOp",EDGE,"E133"),sQuery(id+"F0.wireOp",EDGE,"E134"),sQuery(id+"F0.wireOp",EDGE,"E135"),sQuery(id+"F0.wireOp",EDGE,"E136"),sQuery(id+"F0.wireOp",EDGE,"E137"),sQuery(id+"F0.wireOp",EDGE,"E138"),sQuery(id+"F0.wireOp",EDGE,"E139"),sQuery(id+"F0.wireOp",EDGE,"E140"),sQuery(id+"F0.wireOp",EDGE,"E141"),sQuery(id+"F0.wireOp",EDGE,"E142"),sQuery(id+"F0.wireOp",EDGE,"E143"),sQuery(id+"F0.wireOp",EDGE,"E144"),sQuery(id+"F0.wireOp",EDGE,"E145"),sQuery(id+"F0.wireOp",EDGE,"E146"),sQuery(id+"F0.wireOp",EDGE,"E147"),sQuery(id+"F0.wireOp",EDGE,"E148"),sQuery(id+"F0.wireOp",EDGE,"E149"),sQuery(id+"F0.wireOp",EDGE,"E150"),sQuery(id+"F0.wireOp",EDGE,"E151"),sQuery(id+"F0.wireOp",EDGE,"E152"),sQuery(id+"F0.wireOp",EDGE,"E153"),sQuery(id+"F0.wireOp",EDGE,"E154"),sQuery(id+"F0.wireOp",EDGE,"E155"),sQuery(id+"F0.wireOp",EDGE,"E156"),sQuery(id+"F0.wireOp",EDGE,"E157"),sQuery(id+"F0.wireOp",EDGE,"E158"),sQuery(id+"F0.wireOp",EDGE,"E159"),sQuery(id+"F0.wireOp",EDGE,"E160"),sQuery(id+"F0.wireOp",EDGE,"E161"),sQuery(id+"F0.wireOp",EDGE,"E162"),sQuery(id+"F0.wireOp",EDGE,"E163"),sQuery(id+"F0.wireOp",EDGE,"E163"),sQuery(id+"F0.wireOp",EDGE,"E164"),sQuery(id+"F0.wireOp",EDGE,"E165"),sQuery(id+"F0.wireOp",EDGE,"E166"),sQuery(id+"F0.wireOp",EDGE,"E167"),sQuery(id+"F0.wireOp",EDGE,"E168"),sQuery(id+"F0.wireOp",EDGE,"E169"),sQuery(id+"F0.wireOp",EDGE,"E170"),sQuery(id+"F0.wireOp",EDGE,"E171"),sQuery(id+"F0.wireOp",EDGE,"E172"),sQuery(id+"F0.wireOp",EDGE,"E173"),sQuery(id+"F0.wireOp",EDGE,"E174"),sQuery(id+"F0.wireOp",EDGE,"E175"),sQuery(id+"F0.wireOp",EDGE,"E176"),sQuery(id+"F0.wireOp",EDGE,"E177"),sQuery(id+"F0.wireOp",EDGE,"E178"),sQuery(id+"F0.wireOp",EDGE,"E179"),sQuery(id+"F0.wireOp",EDGE,"E180"),sQuery(id+"F0.wireOp",EDGE,"E181"),sQuery(id+"F0.wireOp",EDGE,"E182"),sQuery(id+"F0.wireOp",EDGE,"E183"),sQuery(id+"F0.wireOp",EDGE,"E184"),sQuery(id+"F0.wireOp",EDGE,"E185"),sQuery(id+"F0.wireOp",EDGE,"E186"),sQuery(id+"F0.wireOp",EDGE,"E187"),sQuery(id+"F0.wireOp",EDGE,"E188"),sQuery(id+"F0.wireOp",EDGE,"E189"),sQuery(id+"F0.wireOp",EDGE,"E190"),sQuery(id+"F0.wireOp",EDGE,"E191"),sQuery(id+"F0.wireOp",EDGE,"E192"),sQuery(id+"F0.wireOp",EDGE,"E193"),sQuery(id+"F0.wireOp",EDGE,"E194"),sQuery(id+"F0.wireOp",EDGE,"E195"),sQuery(id+"F0.wireOp",EDGE,"E196"),sQuery(id+"F0.wireOp",EDGE,"E197"),sQuery(id+"F0.wireOp",EDGE,"E198"),sQuery(id+"F0.wireOp",EDGE,"E199"),sQuery(id+"F0.wireOp",EDGE,"E200"),sQuery(id+"F0.wireOp",EDGE,"E201"),sQuery(id+"F0.wireOp",EDGE,"E202"),sQuery(id+"F0.wireOp",EDGE,"E203"),sQuery(id+"F0.wireOp",EDGE,"E204"),sQuery(id+"F0.wireOp",EDGE,"E205"),sQuery(id+"F0.wireOp",EDGE,"E206"),sQuery(id+"F0.wireOp",EDGE,"E207"),sQuery(id+"F0.wireOp",EDGE,"E208"),sQuery(id+"F0.wireOp",EDGE,"E209"),sQuery(id+"F0.wireOp",EDGE,"E210"),sQuery(id+"F0.wireOp",EDGE,"E211"),sQuery(id+"F0.wireOp",EDGE,"E212"),sQuery(id+"F0.wireOp",EDGE,"E213"),sQuery(id+"F0.wireOp",EDGE,"E214"),sQuery(id+"F0.wireOp",EDGE,"E215"),sQuery(id+"F0.wireOp",EDGE,"E216"),sQuery(id+"F0.wireOp",EDGE,"E217"),sQuery(id+"F0.wireOp",EDGE,"E218"),sQuery(id+"F0.wireOp",EDGE,"E219"),sQuery(id+"F0.wireOp",EDGE,"E220"),sQuery(id+"F0.wireOp",EDGE,"E221"),sQuery(id+"F0.wireOp",EDGE,"E222"),sQuery(id+"F0.wireOp",EDGE,"E223"),sQuery(id+"F0.wireOp",EDGE,"E224"),sQuery(id+"F0.wireOp",EDGE,"E225"),sQuery(id+"F0.wireOp",EDGE,"E226"),sQuery(id+"F0.wireOp",EDGE,"E227"),sQuery(id+"F0.wireOp",EDGE,"E228"),sQuery(id+"F0.wireOp",EDGE,"E229"),sQuery(id+"F0.wireOp",EDGE,"E230"),sQuery(id+"F0.wireOp",EDGE,"E231"),sQuery(id+"F0.wireOp",EDGE,"E232"),sQuery(id+"F0.wireOp",EDGE,"E233"),sQuery(id+"F0.wireOp",EDGE,"E234"),sQuery(id+"F0.wireOp",EDGE,"E235"),sQuery(id+"F0.wireOp",EDGE,"E236"),sQuery(id+"F0.wireOp",EDGE,"E237"),sQuery(id+"F0.wireOp",EDGE,"E238"),sQuery(id+"F0.wireOp",EDGE,"E239"),sQuery(id+"F0.wireOp",EDGE,"E240"),sQuery(id+"F0.wireOp",EDGE,"E241"),sQuery(id+"F0.wireOp",EDGE,"E242"),sQuery(id+"F0.wireOp",EDGE,"E243"),sQuery(id+"F0.wireOp",EDGE,"E244"),sQuery(id+"F0.wireOp",EDGE,"E245"),sQuery(id+"F0.wireOp",EDGE,"E246"),sQuery(id+"F0.wireOp",EDGE,"E247"),sQuery(id+"F0.wireOp",EDGE,"E248"),sQuery(id+"F0.wireOp",EDGE,"E249"),sQuery(id+"F0.wireOp",EDGE,"E250"),sQuery(id+"F0.wireOp",EDGE,"E251"),sQuery(id+"F0.wireOp",EDGE,"E252"),sQuery(id+"F0.wireOp",EDGE,"E253"),sQuery(id+"F0.wireOp",EDGE,"E254"),sQuery(id+"F0.wireOp",EDGE,"E255"),sQuery(id+"F0.wireOp",EDGE,"E256"),sQuery(id+"F0.wireOp",EDGE,"E257"),sQuery(id+"F0.wireOp",EDGE,"E258"),sQuery(id+"F0.wireOp",EDGE,"E259"),sQuery(id+"F0.wireOp",EDGE,"E260"),sQuery(id+"F0.wireOp",EDGE,"E261"),sQuery(id+"F0.wireOp",EDGE,"E262"),sQuery(id+"F0.wireOp",EDGE,"E263"),sQuery(id+"F0.wireOp",EDGE,"E264"),sQuery(id+"F0.wireOp",EDGE,"E265"),sQuery(id+"F0.wireOp",EDGE,"E266"),sQuery(id+"F0.wireOp",EDGE,"E267"),sQuery(id+"F0.wireOp",EDGE,"E268"),sQuery(id+"F0.wireOp",EDGE,"E269"),sQuery(id+"F0.wireOp",EDGE,"E270"),sQuery(id+"F0.wireOp",EDGE,"E271"),sQuery(id+"F0.wireOp",EDGE,"E272"),sQuery(id+"F0.wireOp",EDGE,"E273"),sQuery(id+"F0.wireOp",EDGE,"E274"),sQuery(id+"F0.wireOp",EDGE,"E275"),sQuery(id+"F0.wireOp",EDGE,"E276"),sQuery(id+"F0.wireOp",EDGE,"E277"),sQuery(id+"F0.wireOp",EDGE,"E278"),sQuery(id+"F0.wireOp",EDGE,"E279"),sQuery(id+"F0.wireOp",EDGE,"E280"),sQuery(id+"F0.wireOp",EDGE,"E281"),sQuery(id+"F0.wireOp",EDGE,"E282"),sQuery(id+"F0.wireOp",EDGE,"E283"),sQuery(id+"F0.wireOp",EDGE,"E284"),sQuery(id+"F0.wireOp",EDGE,"E285"),sQuery(id+"F0.wireOp",EDGE,"E286"),sQuery(id+"F0.wireOp",EDGE,"E287"),sQuery(id+"F0.wireOp",EDGE,"E288"),sQuery(id+"F0.wireOp",EDGE,"E289"),sQuery(id+"F0.wireOp",EDGE,"E290"),sQuery(id+"F0.wireOp",EDGE,"E291"),sQuery(id+"F0.wireOp",EDGE,"E292"),sQuery(id+"F0.wireOp",EDGE,"E293"),sQuery(id+"F0.wireOp",EDGE,"E294"),sQuery(id+"F0.wireOp",EDGE,"E295"),sQuery(id+"F0.wireOp",EDGE,"E296"),sQuery(id+"F0.wireOp",EDGE,"E297"),sQuery(id+"F0.wireOp",EDGE,"E298"),sQuery(id+"F0.wireOp",EDGE,"E299"),sQuery(id+"F0.wireOp",EDGE,"E300"),sQuery(id+"F0.wireOp",EDGE,"E301"),sQuery(id+"F0.wireOp",EDGE,"E302"),sQuery(id+"F0.wireOp",EDGE,"E303"),sQuery(id+"F0.wireOp",EDGE,"E304"),sQuery(id+"F0.wireOp",EDGE,"E305"),sQuery(id+"F0.wireOp",EDGE,"E306"),sQuery(id+"F0.wireOp",EDGE,"E307"),sQuery(id+"F0.wireOp",EDGE,"E308"),sQuery(id+"F0.wireOp",EDGE,"E309"),sQuery(id+"F0.wireOp",EDGE,"E310"),sQuery(id+"F0.wireOp",EDGE,"E311"),sQuery(id+"F0.wireOp",EDGE,"E312"),sQuery(id+"F0.wireOp",EDGE,"E313"),sQuery(id+"F0.wireOp",EDGE,"E314"),sQuery(id+"F0.wireOp",EDGE,"E315"),sQuery(id+"F0.wireOp",EDGE,"E316"),sQuery(id+"F0.wireOp",EDGE,"E317"),sQuery(id+"F0.wireOp",EDGE,"E318"),sQuery(id+"F0.wireOp",EDGE,"E319"),sQuery(id+"F0.wireOp",EDGE,"E320"),sQuery(id+"F0.wireOp",EDGE,"E321"),sQuery(id+"F0.wireOp",EDGE,"E322"),sQuery(id+"F0.wireOp",EDGE,"E323"),sQuery(id+"F0.wireOp",EDGE,"E324"),sQuery(id+"F0.wireOp",EDGE,"E325"),sQuery(id+"F0.wireOp",EDGE,"E326"),sQuery(id+"F0.wireOp",EDGE,"E327"),sQuery(id+"F0.wireOp",EDGE,"E328"),sQuery(id+"F0.wireOp",EDGE,"E329"),sQuery(id+"F0.wireOp",EDGE,"E330"),sQuery(id+"F0.wireOp",EDGE,"E331"),sQuery(id+"F0.wireOp",EDGE,"E332"),sQuery(id+"F0.wireOp",EDGE,"E333"),sQuery(id+"F0.wireOp",EDGE,"E334"),sQuery(id+"F0.wireOp",EDGE,"E335"),sQuery(id+"F0.wireOp",EDGE,"E336"),sQuery(id+"F0.wireOp",EDGE,"E337"),sQuery(id+"F0.wireOp",EDGE,"E338"),sQuery(id+"F0.wireOp",EDGE,"E339"),sQuery(id+"F0.wireOp",EDGE,"E340"),sQuery(id+"F0.wireOp",EDGE,"E341"),sQuery(id+"F0.wireOp",EDGE,"E342"),sQuery(id+"F0.wireOp",EDGE,"E343"),sQuery(id+"F0.wireOp",EDGE,"E344"),sQuery(id+"F0.wireOp",EDGE,"E345"),sQuery(id+"F0.wireOp",EDGE,"E346"),sQuery(id+"F0.wireOp",EDGE,"E347"),sQuery(id+"F0.wireOp",EDGE,"E348"),sQuery(id+"F0.wireOp",EDGE,"E349"),sQuery(id+"F0.wireOp",EDGE,"E350"),sQuery(id+"F0.wireOp",EDGE,"E351"),sQuery(id+"F0.wireOp",EDGE,"E352"),sQuery(id+"F0.wireOp",EDGE,"E353"),sQuery(id+"F0.wireOp",EDGE,"E354"),sQuery(id+"F0.wireOp",EDGE,"E355"),sQuery(id+"F0.wireOp",EDGE,"E356"),sQuery(id+"F0.wireOp",EDGE,"E357"),sQuery(id+"F0.wireOp",EDGE,"E358"),sQuery(id+"F0.wireOp",EDGE,"E359"),sQuery(id+"F0.wireOp",EDGE,"E360"),sQuery(id+"F0.wireOp",EDGE,"E361"),sQuery(id+"F0.wireOp",EDGE,"E362"),sQuery(id+"F0.wireOp",EDGE,"E363"),sQuery(id+"F0.wireOp",EDGE,"E364"),sQuery(id+"F0.wireOp",EDGE,"E365"),sQuery(id+"F0.wireOp",EDGE,"E366"),sQuery(id+"F0.wireOp",EDGE,"E367"),sQuery(id+"F0.wireOp",EDGE,"E368"),sQuery(id+"F0.wireOp",EDGE,"E369"),sQuery(id+"F0.wireOp",EDGE,"E370"),sQuery(id+"F0.wireOp",EDGE,"E371"),sQuery(id+"F0.wireOp",EDGE,"E372"),sQuery(id+"F0.wireOp",EDGE,"E373"),sQuery(id+"F0.wireOp",EDGE,"E374"),sQuery(id+"F0.wireOp",EDGE,"E375"),sQuery(id+"F0.wireOp",EDGE,"E376"),sQuery(id+"F0.wireOp",EDGE,"E377"),sQuery(id+"F0.wireOp",EDGE,"E378"),sQuery(id+"F0.wireOp",EDGE,"E379"),sQuery(id+"F0.wireOp",EDGE,"E380"),sQuery(id+"F0.wireOp",EDGE,"E381"),sQuery(id+"F0.wireOp",EDGE,"E382"),sQuery(id+"F0.wireOp",EDGE,"E383"),sQuery(id+"F0.wireOp",EDGE,"E384"),sQuery(id+"F0.wireOp",EDGE,"E385"),sQuery(id+"F0.wireOp",EDGE,"E386"),sQuery(id+"F0.wireOp",EDGE,"E387"),sQuery(id+"F0.wireOp",EDGE,"E388"),sQuery(id+"F0.wireOp",EDGE,"E389"),sQuery(id+"F0.wireOp",EDGE,"E390"),sQuery(id+"F0.wireOp",EDGE,"E391"),sQuery(id+"F0.wireOp",EDGE,"E392"),sQuery(id+"F0.wireOp",EDGE,"E393"),sQuery(id+"F0.wireOp",EDGE,"E394"),sQuery(id+"F0.wireOp",EDGE,"E395"),sQuery(id+"F0.wireOp",EDGE,"E396"),sQuery(id+"F0.wireOp",EDGE,"E397"),sQuery(id+"F0.wireOp",EDGE,"E398"),sQuery(id+"F0.wireOp",EDGE,"E399"),sQuery(id+"F0.wireOp",EDGE,"E400"),sQuery(id+"F0.wireOp",EDGE,"E401"),sQuery(id+"F0.wireOp",EDGE,"E402"),sQuery(id+"F0.wireOp",EDGE,"E403"),sQuery(id+"F0.wireOp",EDGE,"E404"),sQuery(id+"F0.wireOp",EDGE,"E405"),sQuery(id+"F0.wireOp",EDGE,"E406"),sQuery(id+"F0.wireOp",EDGE,"E407"),sQuery(id+"F0.wireOp",EDGE,"E408"),sQuery(id+"F0.wireOp",EDGE,"E409"),sQuery(id+"F0.wireOp",EDGE,"E410"),sQuery(id+"F0.wireOp",EDGE,"E411"),sQuery(id+"F0.wireOp",EDGE,"E412"),sQuery(id+"F0.wireOp",EDGE,"E413"),sQuery(id+"F0.wireOp",EDGE,"E414"),sQuery(id+"F0.wireOp",EDGE,"E415"),sQuery(id+"F0.wireOp",EDGE,"E416"),sQuery(id+"F0.wireOp",EDGE,"E417"),sQuery(id+"F0.wireOp",EDGE,"E418"),sQuery(id+"F0.wireOp",EDGE,"E419"),sQuery(id+"F0.wireOp",EDGE,"E420"),sQuery(id+"F0.wireOp",EDGE,"E421"),sQuery(id+"F0.wireOp",EDGE,"E422"),sQuery(id+"F0.wireOp",EDGE,"E423"),sQuery(id+"F0.wireOp",EDGE,"E424"),sQuery(id+"F0.wireOp",EDGE,"E425"),sQuery(id+"F0.wireOp",EDGE,"E426"),sQuery(id+"F0.wireOp",EDGE,"E426"),sQuery(id+"F0.wireOp",EDGE,"E427"),sQuery(id+"F0.wireOp",EDGE,"E428"),sQuery(id+"F0.wireOp",EDGE,"E429"),sQuery(id+"F0.wireOp",EDGE,"E430"),sQuery(id+"F0.wireOp",EDGE,"E431"),sQuery(id+"F0.wireOp",EDGE,"E432"),sQuery(id+"F0.wireOp",EDGE,"E433"),sQuery(id+"F0.wireOp",EDGE,"E434"),sQuery(id+"F0.wireOp",EDGE,"E435"),sQuery(id+"F0.wireOp",EDGE,"E436"),sQuery(id+"F0.wireOp",EDGE,"E437"),sQuery(id+"F0.wireOp",EDGE,"E438"),sQuery(id+"F0.wireOp",EDGE,"E439"),sQuery(id+"F0.wireOp",EDGE,"E440"),sQuery(id+"F0.wireOp",EDGE,"E441"),sQuery(id+"F0.wireOp",EDGE,"E442"),sQuery(id+"F0.wireOp",EDGE,"E443"),sQuery(id+"F0.wireOp",EDGE,"E444"),sQuery(id+"F0.wireOp",EDGE,"E445"),sQuery(id+"F0.wireOp",EDGE,"E446"),sQuery(id+"F0.wireOp",EDGE,"E447"),sQuery(id+"F0.wireOp",EDGE,"E448"),sQuery(id+"F0.wireOp",EDGE,"E449"),sQuery(id+"F0.wireOp",EDGE,"E450"),sQuery(id+"F0.wireOp",EDGE,"E451"),sQuery(id+"F0.wireOp",EDGE,"E452"),sQuery(id+"F0.wireOp",EDGE,"E453"),sQuery(id+"F0.wireOp",EDGE,"E454"),sQuery(id+"F0.wireOp",EDGE,"E455"),sQuery(id+"F0.wireOp",EDGE,"E456"),sQuery(id+"F0.wireOp",EDGE,"E457"),sQuery(id+"F0.wireOp",EDGE,"E458"),sQuery(id+"F0.wireOp",EDGE,"E459"),sQuery(id+"F0.wireOp",EDGE,"E460"),sQuery(id+"F0.wireOp",EDGE,"E461"),sQuery(id+"F0.wireOp",EDGE,"E462"),sQuery(id+"F0.wireOp",EDGE,"E463"),sQuery(id+"F0.wireOp",EDGE,"E464"),sQuery(id+"F0.wireOp",EDGE,"E465"),sQuery(id+"F0.wireOp",EDGE,"E466"),sQuery(id+"F0.wireOp",EDGE,"E467"),sQuery(id+"F0.wireOp",EDGE,"E468"),sQuery(id+"F0.wireOp",EDGE,"E469"),sQuery(id+"F0.wireOp",EDGE,"E470"),sQuery(id+"F0.wireOp",EDGE,"E471"),sQuery(id+"F0.wireOp",EDGE,"E472"),sQuery(id+"F0.wireOp",EDGE,"E473"),sQuery(id+"F0.wireOp",EDGE,"E474"),sQuery(id+"F0.wireOp",EDGE,"E475"),sQuery(id+"F0.wireOp",EDGE,"E476"),sQuery(id+"F0.wireOp",EDGE,"E477"),sQuery(id+"F0.wireOp",EDGE,"E478"),sQuery(id+"F0.wireOp",EDGE,"E479"),sQuery(id+"F0.wireOp",EDGE,"E480"),sQuery(id+"F0.wireOp",EDGE,"E481"),sQuery(id+"F0.wireOp",EDGE,"E482"),sQuery(id+"F0.wireOp",EDGE,"E483"),sQuery(id+"F0.wireOp",EDGE,"E484"),sQuery(id+"F0.wireOp",EDGE,"E485"),sQuery(id+"F0.wireOp",EDGE,"E486"),sQuery(id+"F0.wireOp",EDGE,"E487"),sQuery(id+"F0.wireOp",EDGE,"E488"),sQuery(id+"F0.wireOp",EDGE,"E489"),sQuery(id+"F0.wireOp",EDGE,"E490"),sQuery(id+"F0.wireOp",EDGE,"E491"),sQuery(id+"F0.wireOp",EDGE,"E492"),sQuery(id+"F0.wireOp",EDGE,"E493"),sQuery(id+"F0.wireOp",EDGE,"E494"),sQuery(id+"F0.wireOp",EDGE,"E495"),sQuery(id+"F0.wireOp",EDGE,"E496"),sQuery(id+"F0.wireOp",EDGE,"E497"),sQuery(id+"F0.wireOp",EDGE,"E498"),sQuery(id+"F0.wireOp",EDGE,"E499"),sQuery(id+"F0.wireOp",EDGE,"E500"),sQuery(id+"F0.wireOp",EDGE,"E501"),sQuery(id+"F0.wireOp",EDGE,"E502"),sQuery(id+"F0.wireOp",EDGE,"E503"),sQuery(id+"F0.wireOp",EDGE,"E504"),sQuery(id+"F0.wireOp",EDGE,"E505"),sQuery(id+"F0.wireOp",EDGE,"E506"),sQuery(id+"F0.wireOp",EDGE,"E507"),sQuery(id+"F0.wireOp",EDGE,"E508"),sQuery(id+"F0.wireOp",EDGE,"E509"),sQuery(id+"F0.wireOp",EDGE,"E510"),sQuery(id+"F0.wireOp",EDGE,"E511"),sQuery(id+"F0.wireOp",EDGE,"E512"),sQuery(id+"F0.wireOp",EDGE,"E513"),sQuery(id+"F0.wireOp",EDGE,"E514"),sQuery(id+"F0.wireOp",EDGE,"E515"),sQuery(id+"F0.wireOp",EDGE,"E516"),sQuery(id+"F0.wireOp",EDGE,"E517"),sQuery(id+"F0.wireOp",EDGE,"E518"),sQuery(id+"F0.wireOp",EDGE,"E519"),sQuery(id+"F0.wireOp",EDGE,"E520"),sQuery(id+"F0.wireOp",EDGE,"E521"),sQuery(id+"F0.wireOp",EDGE,"E522"),sQuery(id+"F0.wireOp",EDGE,"E523"),sQuery(id+"F0.wireOp",EDGE,"E524"),sQuery(id+"F0.wireOp",EDGE,"E525"),sQuery(id+"F0.wireOp",EDGE,"E526"),sQuery(id+"F0.wireOp",EDGE,"E527"),sQuery(id+"F0.wireOp",EDGE,"E528"),sQuery(id+"F0.wireOp",EDGE,"E529"),sQuery(id+"F0.wireOp",EDGE,"E530"),sQuery(id+"F0.wireOp",EDGE,"E531"),sQuery(id+"F0.wireOp",EDGE,"E532"),sQuery(id+"F0.wireOp",EDGE,"E533"),sQuery(id+"F0.wireOp",EDGE,"E534"),sQuery(id+"F0.wireOp",EDGE,"E535"),sQuery(id+"F0.wireOp",EDGE,"E536"),sQuery(id+"F0.wireOp",EDGE,"E537"),sQuery(id+"F0.wireOp",EDGE,"E538"),sQuery(id+"F0.wireOp",EDGE,"E539"),sQuery(id+"F0.wireOp",EDGE,"E540"),sQuery(id+"F0.wireOp",EDGE,"E541"),sQuery(id+"F0.wireOp",EDGE,"E542"),sQuery(id+"F0.wireOp",EDGE,"E543"),sQuery(id+"F0.wireOp",EDGE,"E544"),sQuery(id+"F0.wireOp",EDGE,"E545"),sQuery(id+"F0.wireOp",EDGE,"E546"),sQuery(id+"F0.wireOp",EDGE,"E547"),sQuery(id+"F0.wireOp",EDGE,"E548"),sQuery(id+"F0.wireOp",EDGE,"E549"),sQuery(id+"F0.wireOp",EDGE,"E550"),sQuery(id+"F0.wireOp",EDGE,"E551"),sQuery(id+"F0.wireOp",EDGE,"E552"),sQuery(id+"F0.wireOp",EDGE,"E553"),sQuery(id+"F0.wireOp",EDGE,"E554"),sQuery(id+"F0.wireOp",EDGE,"E555"),sQuery(id+"F0.wireOp",EDGE,"E556"),sQuery(id+"F0.wireOp",EDGE,"E557"),sQuery(id+"F0.wireOp",EDGE,"E558"),sQuery(id+"F0.wireOp",EDGE,"E559"),sQuery(id+"F0.wireOp",EDGE,"E560"),sQuery(id+"F0.wireOp",EDGE,"E561"),sQuery(id+"F0.wireOp",EDGE,"E562"),sQuery(id+"F0.wireOp",EDGE,"E563"),sQuery(id+"F0.wireOp",EDGE,"E564"),sQuery(id+"F0.wireOp",EDGE,"E565"),sQuery(id+"F0.wireOp",EDGE,"E566"),sQuery(id+"F0.wireOp",EDGE,"E567"),sQuery(id+"F0.wireOp",EDGE,"E568"),sQuery(id+"F0.wireOp",EDGE,"E569"),sQuery(id+"F0.wireOp",EDGE,"E570"),sQuery(id+"F0.wireOp",EDGE,"E571"),sQuery(id+"F0.wireOp",EDGE,"E572"),sQuery(id+"F0.wireOp",EDGE,"E573"),sQuery(id+"F0.wireOp",EDGE,"E574"),sQuery(id+"F0.wireOp",EDGE,"E575"),sQuery(id+"F0.wireOp",EDGE,"E576"),sQuery(id+"F0.wireOp",EDGE,"E577"),sQuery(id+"F0.wireOp",EDGE,"E578"),sQuery(id+"F0.wireOp",EDGE,"E579"),sQuery(id+"F0.wireOp",EDGE,"E580"),sQuery(id+"F0.wireOp",EDGE,"E581"),sQuery(id+"F0.wireOp",EDGE,"E582"),sQuery(id+"F0.wireOp",EDGE,"E583"),sQuery(id+"F0.wireOp",EDGE,"E584"),sQuery(id+"F0.wireOp",EDGE,"E585"),sQuery(id+"F0.wireOp",EDGE,"E586"),sQuery(id+"F0.wireOp",EDGE,"E587"),sQuery(id+"F0.wireOp",EDGE,"E588"),sQuery(id+"F0.wireOp",EDGE,"E589"),sQuery(id+"F0.wireOp",EDGE,"E590"),sQuery(id+"F0.wireOp",EDGE,"E591"),sQuery(id+"F0.wireOp",EDGE,"E592"),sQuery(id+"F0.wireOp",EDGE,"E593"),sQuery(id+"F0.wireOp",EDGE,"E594"),sQuery(id+"F0.wireOp",EDGE,"E595"),sQuery(id+"F0.wireOp",EDGE,"E596"),sQuery(id+"F0.wireOp",EDGE,"E597"),sQuery(id+"F0.wireOp",EDGE,"E598"),sQuery(id+"F0.wireOp",EDGE,"E599"),sQuery(id+"F0.wireOp",EDGE,"E600"),sQuery(id+"F0.wireOp",EDGE,"E601"),sQuery(id+"F0.wireOp",EDGE,"E602"),sQuery(id+"F0.wireOp",EDGE,"E603"),sQuery(id+"F0.wireOp",EDGE,"E604"),sQuery(id+"F0.wireOp",EDGE,"E605"),sQuery(id+"F0.wireOp",EDGE,"E606"),sQuery(id+"F0.wireOp",EDGE,"E607"),sQuery(id+"F0.wireOp",EDGE,"E608"),sQuery(id+"F0.wireOp",EDGE,"E609"),sQuery(id+"F0.wireOp",EDGE,"E610"),sQuery(id+"F0.wireOp",EDGE,"E611"),sQuery(id+"F0.wireOp",EDGE,"E612"),sQuery(id+"F0.wireOp",EDGE,"E613"),sQuery(id+"F0.wireOp",EDGE,"E614"),sQuery(id+"F0.wireOp",EDGE,"E615"),sQuery(id+"F0.wireOp",EDGE,"E616"),sQuery(id+"F0.wireOp",EDGE,"E617"),sQuery(id+"F0.wireOp",EDGE,"E618"),sQuery(id+"F0.wireOp",EDGE,"E619")])],"isStart":false});
            fillet(context, id + "F2", {"entities" : qUnion([Q0]), "radius" : 0.1 * mm, "tangentPropagation" : true, "allowEdgeOverflow" : false});
        }
    });
